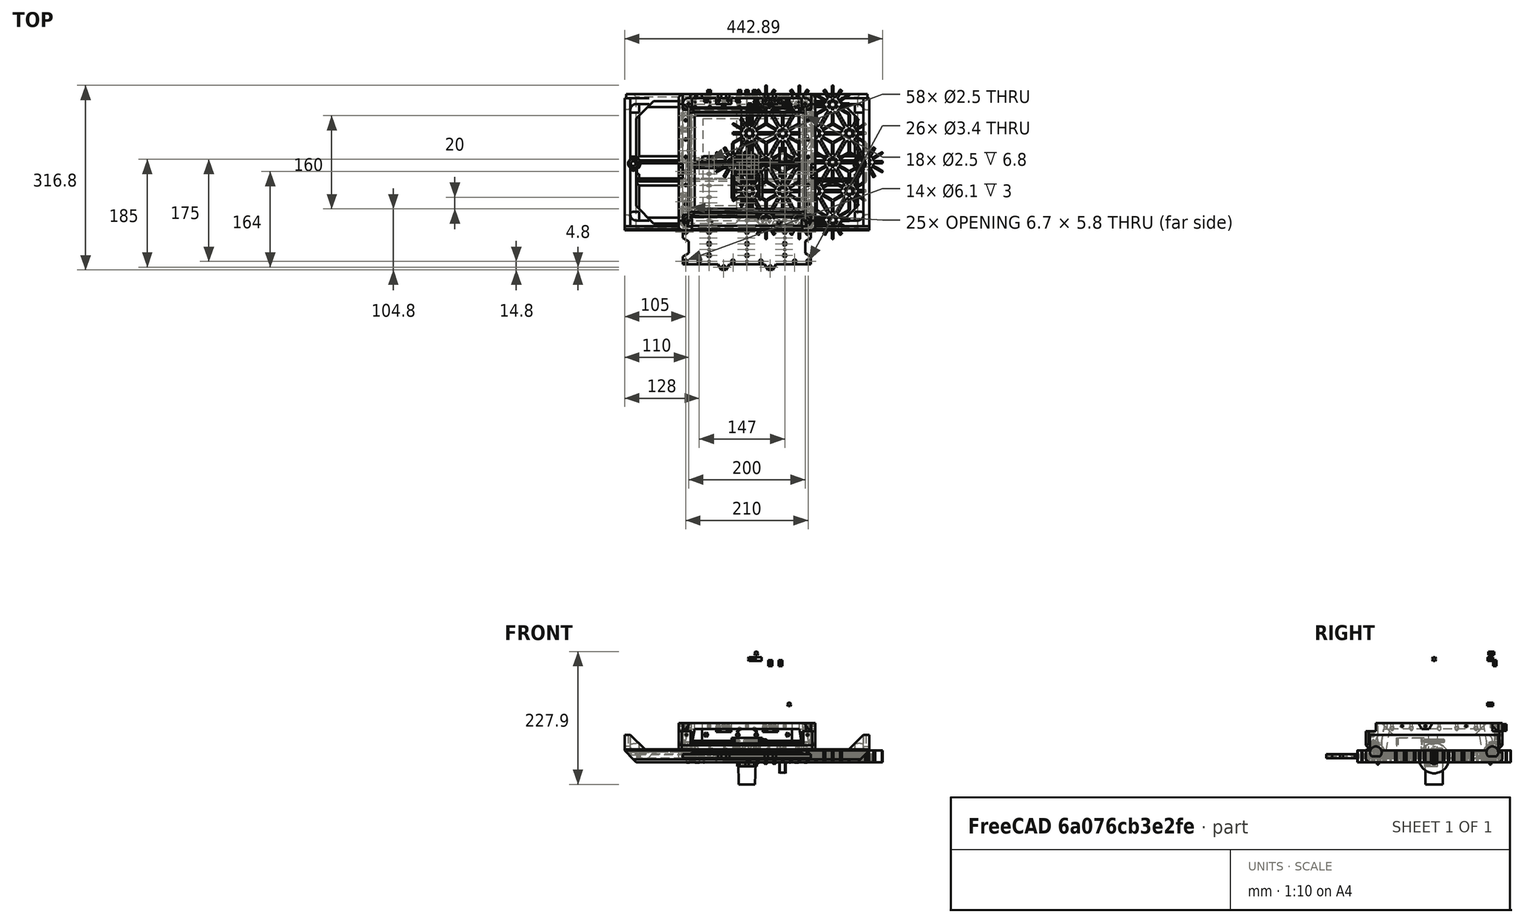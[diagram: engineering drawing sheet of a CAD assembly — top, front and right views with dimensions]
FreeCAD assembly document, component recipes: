
FREECAD ASSEMBLY — COMPONENT RECIPES ("miniXY-Frame")

This assembly document has 23 components, labeled P0..P22 below (a component is one placed body or linked part). 20 of them carry a construction recipe — the FreeCAD feature program that regenerates the part from scratch, quoted from this document or its linked companion documents; the rest are supplied as boundary geometry only. No exploded tour is included for this assembly.
NOTE — document 2 of 3 of this assembly tour. The two overview renders and the header above are repeated from document 1; the component sections below continue where the previous document stopped.
COMPONENT P8 — recipe-attached ("RearPanel", modeled in this document).
Construction recipe (the document's own serialized feature program — sketch geometry with constraints, then the solid features built on it; lengths are millimeters unless a unit is written):

FEATURE [Sketcher::SketchObject] Sketch089
  FullyConstrained = true
  MapMode = 5
  Support = -> [XY_Plane012]
  expr: Constraints[100] = <<Variables>>.FittingGap / 2
  expr: Constraints[101] = <<Variables>>.FittingGap / 2
  expr: Constraints[130] = -<<Variables>>.GantorySpacing / 2
  expr: Constraints[131] = 10 - <<Variables>>.FittingGap
  expr: Constraints[56] = 10 - <<Variables>>.FittingGap
  expr: Constraints[62] = <<Variables>>.FittingGap / 2
  expr: Constraints[63] = <<Variables>>.FittingGap / 2
  expr: Constraints[96] = <<Variables>>.FittingGap / 2
  expr: Constraints[97] = <<Variables>>.FittingGap / 2
  expr: Constraints[98] = <<Variables>>.FittingGap / 2
  expr: Constraints[99] = <<Variables>>.FittingGap / 2
  sketch-geometry (64):
    g0: LineSegment StartX=-109.8 StartY=0 StartZ=0 EndX=-109.8 EndY=-26.242 EndZ=0
    g1: LineSegment StartX=-109.8 StartY=-26.242 StartZ=0 EndX=-100 EndY=-31.9 EndZ=0
    g2: LineSegment StartX=-100 StartY=-52.1 StartZ=0 EndX=-109.8 EndY=-57.758 EndZ=0
    g3: LineSegment StartX=-109.8 StartY=-57.758 StartZ=0 EndX=-109.8 EndY=-78.242 EndZ=0
    g4: LineSegment StartX=-109.8 StartY=-78.242 StartZ=0 EndX=-100 EndY=-83.9 EndZ=0
    g5: LineSegment StartX=-100 StartY=-104.1 StartZ=0 EndX=-109.8 EndY=-109.758 EndZ=0
    g6: LineSegment StartX=-109.8 StartY=-109.758 StartZ=0 EndX=-109.8 EndY=-130.242 EndZ=0
    g7: LineSegment StartX=-109.8 StartY=-130.242 StartZ=0 EndX=-100 EndY=-135.9 EndZ=0
    g8: LineSegment StartX=-100 StartY=-156.1 StartZ=0 EndX=-109.8 EndY=-161.758 EndZ=0
    g9: LineSegment StartX=-109.8 StartY=-161.758 StartZ=0 EndX=-109.8 EndY=-175 EndZ=0
    g10: LineSegment StartX=-49.9 StartY=-175 StartZ=0 EndX=-44.242 EndY=-184.8 EndZ=0
    g11: LineSegment StartX=-44.242 StartY=-184.8 StartZ=0 EndX=-35.758 EndY=-184.8 EndZ=0
    g12: LineSegment StartX=-35.758 StartY=-184.8 StartZ=0 EndX=-30.1 EndY=-175 EndZ=0
    g13: LineSegment StartX=30.1 StartY=-175 StartZ=0 EndX=35.758 EndY=-184.8 EndZ=0
    g14: LineSegment StartX=35.758 StartY=-184.8 StartZ=0 EndX=44.242 EndY=-184.8 EndZ=0
    g15: LineSegment StartX=44.242 StartY=-184.8 StartZ=0 EndX=49.9 EndY=-175 EndZ=0
    g16: LineSegment StartX=49.9 StartY=-175 StartZ=0 EndX=109.8 EndY=-175 EndZ=0
    g17: LineSegment StartX=109.8 StartY=-175 StartZ=0 EndX=109.8 EndY=-161.758 EndZ=0
    g18: LineSegment StartX=109.8 StartY=-161.758 StartZ=0 EndX=100 EndY=-156.1 EndZ=0
    g19: LineSegment StartX=100 StartY=-156.1 StartZ=0 EndX=100 EndY=-135.9 EndZ=0
    g20: LineSegment StartX=100 StartY=-135.9 StartZ=0 EndX=109.8 EndY=-130.242 EndZ=0
    g21: LineSegment StartX=109.8 StartY=-130.242 StartZ=0 EndX=109.8 EndY=-109.758 EndZ=0
    g22: LineSegment StartX=109.8 StartY=-109.758 StartZ=0 EndX=100 EndY=-104.1 EndZ=0
    g23: LineSegment StartX=100 StartY=-104.1 StartZ=0 EndX=100 EndY=-83.9 EndZ=0
    g24: LineSegment StartX=100 StartY=-83.9 StartZ=0 EndX=109.8 EndY=-78.242 EndZ=0
    g25: LineSegment StartX=109.8 StartY=-78.242 StartZ=0 EndX=109.8 EndY=-57.758 EndZ=0
    g26: LineSegment StartX=109.8 StartY=-57.758 StartZ=0 EndX=100 EndY=-52.1 EndZ=0
    g27: LineSegment StartX=100 StartY=-52.1 StartZ=0 EndX=100 EndY=-31.9 EndZ=0
    g28: LineSegment StartX=100 StartY=-31.9 StartZ=0 EndX=109.8 EndY=-26.242 EndZ=0
    g29: LineSegment StartX=109.8 StartY=-26.242 StartZ=0 EndX=109.8 EndY=0 EndZ=0
    g30: LineSegment StartX=109.8 StartY=0 StartZ=0 EndX=-109.8 EndY=0 EndZ=0
    g31: LineSegment StartX=-30.1 StartY=-175 StartZ=0 EndX=30.1 EndY=-175 EndZ=0
    g32: LineSegment StartX=-109.8 StartY=-175 StartZ=0 EndX=-49.9 EndY=-175 EndZ=0
    g33: LineSegment StartX=-100 StartY=-31.9 StartZ=0 EndX=-100 EndY=-52.1 EndZ=0
    g34: LineSegment StartX=-100 StartY=-83.9 StartZ=0 EndX=-100 EndY=-104.1 EndZ=0
    g35: LineSegment StartX=-100 StartY=-135.9 StartZ=0 EndX=-100 EndY=-156.1 EndZ=0
    g36: LineSegment StartX=-100 StartY=0 StartZ=0 EndX=-100 EndY=-235 EndZ=0
    g37: LineSegment StartX=-109.8 StartY=0 StartZ=0 EndX=-109.8 EndY=-235 EndZ=0
    g38: LineSegment StartX=-117.5 StartY=-175 StartZ=0 EndX=117.5 EndY=-175 EndZ=0
    g39: LineSegment StartX=-117.5 StartY=-184.8 StartZ=0 EndX=117.5 EndY=-184.8 EndZ=0
    g40: GeomPoint X=-30 Y=-175 Z=0
    g41: GeomPoint X=-50 Y=-175 Z=0
    g42: GeomPoint X=-100 Y=-32 Z=0
    g43: GeomPoint X=-100 Y=-52 Z=0
    g44: GeomPoint X=-100 Y=-84 Z=0
    g45: GeomPoint X=-100 Y=-104 Z=0
    g46: GeomPoint X=-100 Y=-136 Z=0
    g47: GeomPoint X=-100 Y=-156 Z=0
    g48: Circle CenterX=-40 CenterY=-180 CenterZ=0 NormalX=0 NormalY=0 NormalZ=1 AngleXU=0 Radius=1.5
    g49: Circle CenterX=40 CenterY=-180 CenterZ=0 NormalX=0 NormalY=0 NormalZ=1 AngleXU=0 Radius=1.5
    g50: LineSegment StartX=-117.5 StartY=-170 StartZ=0 EndX=117.5 EndY=-170 EndZ=0
    g51: Circle CenterX=-24 CenterY=-170 CenterZ=0 NormalX=0 NormalY=0 NormalZ=1 AngleXU=0 Radius=1.5
    g52: Circle CenterX=24 CenterY=-170 CenterZ=0 NormalX=0 NormalY=0 NormalZ=1 AngleXU=0 Radius=1.5
    g53: Circle CenterX=-82 CenterY=-170 CenterZ=0 NormalX=0 NormalY=0 NormalZ=1 AngleXU=0 Radius=1.5
    g54: Circle CenterX=82 CenterY=-170 CenterZ=0 NormalX=0 NormalY=0 NormalZ=1 AngleXU=0 Radius=1.5
    g55: LineSegment StartX=-105 StartY=0 StartZ=0 EndX=-105 EndY=-235 EndZ=0
    g56: Circle CenterX=-105 CenterY=-16 CenterZ=0 NormalX=0 NormalY=0 NormalZ=1 AngleXU=0 Radius=1.5
    g57: Circle CenterX=105 CenterY=-16 CenterZ=0 NormalX=0 NormalY=0 NormalZ=1 AngleXU=0 Radius=1.5
    g58: Circle CenterX=-105 CenterY=-68 CenterZ=0 NormalX=0 NormalY=0 NormalZ=1 AngleXU=0 Radius=1.5
    g59: Circle CenterX=105 CenterY=-68 CenterZ=0 NormalX=0 NormalY=0 NormalZ=1 AngleXU=0 Radius=1.5
    g60: Circle CenterX=-105 CenterY=-120 CenterZ=0 NormalX=0 NormalY=0 NormalZ=1 AngleXU=0 Radius=1.5
    g61: Circle CenterX=105 CenterY=-120 CenterZ=0 NormalX=0 NormalY=0 NormalZ=1 AngleXU=0 Radius=1.5
    g62: Circle CenterX=-105 CenterY=-170 CenterZ=0 NormalX=0 NormalY=0 NormalZ=1 AngleXU=0 Radius=1.5
    g63: Circle CenterX=105 CenterY=-170 CenterZ=0 NormalX=0 NormalY=0 NormalZ=1 AngleXU=0 Radius=1.5
  constraints (156):
    c: Coincident(g0,g1)
    c: Coincident(g2,g3)
    c: Coincident(g3,g4)
    c: Coincident(g5,g6)
    c: Coincident(g6,g7)
    c: Coincident(g8,g9)
    c: Coincident(g9,g32)
    c: Coincident(g10,g11)
    c: Coincident(g11,g12)
    c: Coincident(g31,g13)
    c: Coincident(g13,g14)
    c: Coincident(g14,g15)
    c: Coincident(g16,g17)
    c: Coincident(g17,g18)
    c: Coincident(g18,g19)
    c: Coincident(g19,g20)
    c: Coincident(g20,g21)
    c: Coincident(g21,g22)
    c: Coincident(g22,g23)
    c: Coincident(g23,g24)
    c: Coincident(g24,g25)
    c: Coincident(g25,g26)
    c: Coincident(g26,g27)
    c: Coincident(g27,g28)
    c: Coincident(g28,g29)
    c: Coincident(g29,g30)
    c: Coincident(g30,g0)
    c: Parallel(g1,g4)
    c: Parallel(g1,g7)
    c: Parallel(g2,g5)
    c: Parallel(g2,g8)
    c: Symmetric(g0,g29,g-2)
    c: Symmetric(g0,g28,g-2)
    c: Symmetric(g1,g27,g-2)
    c: Symmetric(g2,g26,g-2)
    c: Symmetric(g2,g25,g-2)
    c: Symmetric(g3,g24,g-2)
    c: Symmetric(g4,g23,g-2)
    c: Symmetric(g5,g22,g-2)
    c: Symmetric(g5,g21,g-2)
    c: Symmetric(g6,g20,g-2)
    c: Symmetric(g7,g19,g-2)
    c: Symmetric(g8,g18,g-2)
    c: Symmetric(g8,g17,g-2)
    c: Symmetric(g9,g16,g-2)
    c: Symmetric(g10,g15,g-2)
    c: Symmetric(g10,g14,g-2)
    c: Symmetric(g11,g13,g-2)
    c: Symmetric(g12,g31,g-2)
    c: Angle(g1) = -0.523599
    c: Angle(g2) = -2.61799
    c: Symmetric(g38,g38,g-2)
    c: Symmetric(g39,g39,g-2)
    c: DistanceX(g39,g39) = 235
    c: Equal(g39,g38)
    c: DistanceY(g38) = -175
    c: DistanceY(g39,g38) = 9.8
    c: Coincident(g31,g12)
    c: PointOnObject(g40,g38)
    c: PointOnObject(g41,g38)
    c: DistanceX(g40) = -30
    c: DistanceX(g41,g40) = 20
    c: DistanceX(g41,g10) = 0.1
    c: DistanceX(g12,g40) = 0.1
    c: PointOnObject(g12,g38)
    c: PointOnObject(g11,g39)
    c: PointOnObject(g10,g39)
    c: PointOnObject(g10,g38)
    c: PointOnObject(g9,g38)
    c: PointOnObject(g42,g36)
    c: PointOnObject(g43,g36)
    c: PointOnObject(g44,g36)
    c: PointOnObject(g45,g36)
    c: PointOnObject(g46,g36)
    c: PointOnObject(g47,g36)
    c: Coincident(g1,g33)
    c: Coincident(g33,g2)
    c: Coincident(g4,g34)
    c: Coincident(g5,g34)
    c: Coincident(g7,g35)
    c: Coincident(g8,g35)
    c: PointOnObject(g9,g37)
    c: PointOnObject(g8,g37)
    c: PointOnObject(g6,g37)
    c: PointOnObject(g5,g37)
    c: PointOnObject(g3,g37)
    c: PointOnObject(g2,g37)
    c: PointOnObject(g0,g37)
    c: PointOnObject(g0,g37)
    c: PointOnObject(g0,g-1)
    c: DistanceY(g42) = -32
    c: DistanceY(g43,g42) = 20
    c: DistanceY(g44,g43) = 32
    c: DistanceY(g45,g44) = 20
    c: DistanceY(g46,g45) = 32
    c: DistanceY(g47,g46) = 20
    c: DistanceY(g42,g1) = 0.1
    c: DistanceY(g2,g43) = 0.1
    c: DistanceY(g44,g4) = 0.1
    c: DistanceY(g5,g45) = 0.1
    c: DistanceY(g46,g7) = 0.1
    c: DistanceY(g8,g47) = 0.1
    c: PointOnObject(g1,g36)
    c: PointOnObject(g2,g36)
    c: PointOnObject(g4,g36)
    c: PointOnObject(g5,g36)
    c: PointOnObject(g7,g36)
    c: PointOnObject(g8,g36)
    c: Coincident(g16,g15)
    c: Coincident(g32,g10)
    c: Angle(g12) = 1.0472
    c: Angle(g10) = -1.0472
    c: Symmetric(g48,g49,g-2)
    c: DistanceX(g48) = -40
    c: DistanceY(g48) = -180
    c: Equal(g48,g49)
    c: Diameter(g48) = 3
    c: Symmetric(g50,g50,g-2)
    c: Equal(g39,g50)
    c: DistanceY(g38,g50) = 5
    c: PointOnObject(g51,g50)
    c: PointOnObject(g53,g50)
    c: Symmetric(g51,g52,g-2)
    c: Symmetric(g53,g54,g-2)
    c: DistanceX(g51) = -24
    c: DistanceX(g53) = -82
    c: Equal(g51,g48)
    c: Equal(g52,g48)
    c: Equal(g53,g48)
    c: Equal(g54,g48)
    c: DistanceX(g36) = -100
    c: DistanceX(g37,g36) = 9.8
    c: Vertical(g36)
    c: Vertical(g37)
    c: PointOnObject(g36,g-1)
    c: PointOnObject(g37,g-1)
    c: DistanceY(g37,g37) = 235
    c: Equal(g37,g36)
    c: PointOnObject(g55,g-1)
    c: Vertical(g55)
    c: Equal(g55,g37)
    c: DistanceX(g55,g36) = 5
    c: PointOnObject(g56,g55)
    c: PointOnObject(g58,g55)
    c: PointOnObject(g60,g55)
    c: PointOnObject(g62,g55)
    c: Symmetric(g56,g57,g-2)
    c: Symmetric(g58,g59,g-2)
    c: Symmetric(g60,g61,g-2)
    c: Symmetric(g62,g63,g-2)
    c: DistanceY(g56) = -16
    c: DistanceY(g58,g56) = 52
    c: DistanceY(g60,g58) = 52
    c: PointOnObject(g62,g50)
    c: Equal(g56, g57-g63) x7
    c: Diameter(g56) = 3
FEATURE [PartDesign::Pad] Pad033
  Direction = (0,0,1)
  Length = 7
  Length2 = 10
  Profile = -> Sketch089
  ReferenceAxis = -> Sketch089 [N_Axis]
  Type = 0
  expr: Length = <<Variables>>.WallThickness
FEATURE [PartDesign::SubShapeBinder] Binder009
  BindCopyOnChange = 0
  BindMode = 0
  ClaimChildren = false
  Context = -> Part005 [Body005.Hole034.Binder009.]
  Fuse = false
  MakeFace = true
  OffsetFill = false
  OffsetIntersection = false
  OffsetJoinType = 0
  OffsetOpenResult = false
  PartialLoad = false
  Placement = pos=(0,0,7) rot=(0,0,1;0rad)
  Relative = true
  Support = -> [Pad033[Sketch089.]]
  _Version = 2
  expr: .Placement.Base.z = <<Variables>>.WallThickness
FEATURE [PartDesign::Hole] Hole034
  BaseFeature = -> Pad033
  CustomThreadClearance = 0
  Depth = 25
  DepthType = 0
  Diameter = 3.4
  DrillForDepth = false
  DrillPoint = 1
  DrillPointAngle = 118
  HoleCutCountersinkAngle = 90
  HoleCutCustomValues = false
  HoleCutDepth = 3
  HoleCutDiameter = 6.1
  HoleCutType = 1
  ModelThread = false
  Profile = -> Binder009
  Tapered = false
  TaperedAngle = 90
  ThreadClass = 0
  ThreadDepth = 25
  ThreadDepthType = 0
  ThreadDirection = 0
  ThreadFit = 0
  ThreadSize = 9
  ThreadType = 1
  Threaded = false
  UseCustomThreadClearance = false
FEATURE [Sketcher::SketchObject] Sketch097
  FullyConstrained = true
  MapMode = 5
  Support = -> [XY_Plane012]
  expr: Constraints[153] = <<Variables>>.GantorySpacing - 70
  sketch-geometry (94):
    g0: Circle CenterX=-65 CenterY=-170 CenterZ=0 NormalX=0 NormalY=0 NormalZ=1 AngleXU=0 Radius=1.5
    g1: Circle CenterX=-65 CenterY=-160 CenterZ=0 NormalX=0 NormalY=0 NormalZ=1 AngleXU=0 Radius=1.5
    g2: LineSegment StartX=-65 StartY=-170 StartZ=0 EndX=-65 EndY=-160 EndZ=0
    g3: Circle CenterX=-65 CenterY=-150 CenterZ=0 NormalX=0 NormalY=0 NormalZ=1 AngleXU=0 Radius=1.5
    g4: LineSegment StartX=-65 StartY=-160 StartZ=0 EndX=-65 EndY=-150 EndZ=0
    g5: Circle CenterX=-65 CenterY=-140 CenterZ=0 NormalX=0 NormalY=0 NormalZ=1 AngleXU=0 Radius=1.5
    g6: LineSegment StartX=-65 StartY=-150 StartZ=0 EndX=-65 EndY=-140 EndZ=0
    g7: Circle CenterX=-65 CenterY=-130 CenterZ=0 NormalX=0 NormalY=0 NormalZ=1 AngleXU=0 Radius=1.5
    g8: LineSegment StartX=-65 StartY=-140 StartZ=0 EndX=-65 EndY=-130 EndZ=0
    g9: Circle CenterX=-65 CenterY=-120 CenterZ=0 NormalX=0 NormalY=0 NormalZ=1 AngleXU=0 Radius=1.5
    g10: LineSegment StartX=-65 StartY=-130 StartZ=0 EndX=-65 EndY=-120 EndZ=0
    g11: Circle CenterX=-65 CenterY=-110 CenterZ=0 NormalX=0 NormalY=0 NormalZ=1 AngleXU=0 Radius=1.5
    g12: LineSegment StartX=-65 StartY=-120 StartZ=0 EndX=-65 EndY=-110 EndZ=0
    g13: Circle CenterX=-65 CenterY=-100 CenterZ=0 NormalX=0 NormalY=0 NormalZ=1 AngleXU=0 Radius=1.5
    g14: LineSegment StartX=-65 StartY=-110 StartZ=0 EndX=-65 EndY=-100 EndZ=0
    g15: Circle CenterX=-65 CenterY=-90 CenterZ=0 NormalX=0 NormalY=0 NormalZ=1 AngleXU=0 Radius=1.5
    g16: LineSegment StartX=-65 StartY=-100 StartZ=0 EndX=-65 EndY=-90 EndZ=0
    g17: Circle CenterX=-65 CenterY=-80 CenterZ=0 NormalX=0 NormalY=0 NormalZ=1 AngleXU=0 Radius=1.5
    g18: LineSegment StartX=-65 StartY=-90 StartZ=0 EndX=-65 EndY=-80 EndZ=0
    g19: Circle CenterX=-65 CenterY=-70 CenterZ=0 NormalX=0 NormalY=0 NormalZ=1 AngleXU=0 Radius=1.5
    g20: LineSegment StartX=-65 StartY=-80 StartZ=0 EndX=-65 EndY=-70 EndZ=0
    g21: Circle CenterX=-65 CenterY=-60 CenterZ=0 NormalX=0 NormalY=0 NormalZ=1 AngleXU=0 Radius=1.5
    g22: LineSegment StartX=-65 StartY=-70 StartZ=0 EndX=-65 EndY=-60 EndZ=0
    g23: Circle CenterX=-65 CenterY=-50 CenterZ=0 NormalX=0 NormalY=0 NormalZ=1 AngleXU=0 Radius=1.5
    g24: LineSegment StartX=-65 StartY=-60 StartZ=0 EndX=-65 EndY=-50 EndZ=0
    g25: Circle CenterX=-65 CenterY=-40 CenterZ=0 NormalX=0 NormalY=0 NormalZ=1 AngleXU=0 Radius=1.5
    g26: LineSegment StartX=-65 StartY=-50 StartZ=0 EndX=-65 EndY=-40 EndZ=0
    g27: Circle CenterX=-65 CenterY=-30 CenterZ=0 NormalX=0 NormalY=0 NormalZ=1 AngleXU=0 Radius=1.5
    g28: LineSegment StartX=-65 StartY=-40 StartZ=0 EndX=-65 EndY=-30 EndZ=0
    g29: Circle CenterX=-65 CenterY=-20 CenterZ=0 NormalX=0 NormalY=0 NormalZ=1 AngleXU=0 Radius=1.5
    g30: LineSegment StartX=-65 StartY=-30 StartZ=0 EndX=-65 EndY=-20 EndZ=0
    g31: Circle CenterX=65 CenterY=-170 CenterZ=0 NormalX=0 NormalY=0 NormalZ=1 AngleXU=0 Radius=1.5
    g32: Circle CenterX=65 CenterY=-160 CenterZ=0 NormalX=0 NormalY=0 NormalZ=1 AngleXU=0 Radius=1.5
    g33: LineSegment StartX=65 StartY=-170 StartZ=0 EndX=65 EndY=-160 EndZ=0
    g34: Circle CenterX=65 CenterY=-150 CenterZ=0 NormalX=0 NormalY=0 NormalZ=1 AngleXU=0 Radius=1.5
    g35: LineSegment StartX=65 StartY=-160 StartZ=0 EndX=65 EndY=-150 EndZ=0
    g36: Circle CenterX=65 CenterY=-140 CenterZ=0 NormalX=0 NormalY=0 NormalZ=1 AngleXU=0 Radius=1.5
    g37: LineSegment StartX=65 StartY=-150 StartZ=0 EndX=65 EndY=-140 EndZ=0
    g38: Circle CenterX=65 CenterY=-130 CenterZ=0 NormalX=0 NormalY=0 NormalZ=1 AngleXU=0 Radius=1.5
    g39: LineSegment StartX=65 StartY=-140 StartZ=0 EndX=65 EndY=-130 EndZ=0
    g40: Circle CenterX=65 CenterY=-120 CenterZ=0 NormalX=0 NormalY=0 NormalZ=1 AngleXU=0 Radius=1.5
    g41: LineSegment StartX=65 StartY=-130 StartZ=0 EndX=65 EndY=-120 EndZ=0
    g42: Circle CenterX=65 CenterY=-110 CenterZ=0 NormalX=0 NormalY=0 NormalZ=1 AngleXU=0 Radius=1.5
    g43: LineSegment StartX=65 StartY=-120 StartZ=0 EndX=65 EndY=-110 EndZ=0
    g44: Circle CenterX=65 CenterY=-100 CenterZ=0 NormalX=0 NormalY=0 NormalZ=1 AngleXU=0 Radius=1.5
    g45: LineSegment StartX=65 StartY=-110 StartZ=0 EndX=65 EndY=-100 EndZ=0
    g46: Circle CenterX=65 CenterY=-90 CenterZ=0 NormalX=0 NormalY=0 NormalZ=1 AngleXU=0 Radius=1.5
    g47: LineSegment StartX=65 StartY=-100 StartZ=0 EndX=65 EndY=-90 EndZ=0
    g48: Circle CenterX=65 CenterY=-80 CenterZ=0 NormalX=0 NormalY=0 NormalZ=1 AngleXU=0 Radius=1.5
    g49: LineSegment StartX=65 StartY=-90 StartZ=0 EndX=65 EndY=-80 EndZ=0
    g50: Circle CenterX=65 CenterY=-70 CenterZ=0 NormalX=0 NormalY=0 NormalZ=1 AngleXU=0 Radius=1.5
    g51: LineSegment StartX=65 StartY=-80 StartZ=0 EndX=65 EndY=-70 EndZ=0
    g52: Circle CenterX=65 CenterY=-60 CenterZ=0 NormalX=0 NormalY=0 NormalZ=1 AngleXU=0 Radius=1.5
    g53: LineSegment StartX=65 StartY=-70 StartZ=0 EndX=65 EndY=-60 EndZ=0
    g54: Circle CenterX=65 CenterY=-50 CenterZ=0 NormalX=0 NormalY=0 NormalZ=1 AngleXU=0 Radius=1.5
    g55: LineSegment StartX=65 StartY=-60 StartZ=0 EndX=65 EndY=-50 EndZ=0
    g56: Circle CenterX=65 CenterY=-40 CenterZ=0 NormalX=0 NormalY=0 NormalZ=1 AngleXU=0 Radius=1.5
    g57: LineSegment StartX=65 StartY=-50 StartZ=0 EndX=65 EndY=-40 EndZ=0
    g58: Circle CenterX=65 CenterY=-30 CenterZ=0 NormalX=0 NormalY=0 NormalZ=1 AngleXU=0 Radius=1.5
    g59: LineSegment StartX=65 StartY=-40 StartZ=0 EndX=65 EndY=-30 EndZ=0
    g60: Circle CenterX=65 CenterY=-20 CenterZ=0 NormalX=0 NormalY=0 NormalZ=1 AngleXU=0 Radius=1.5
    g61: LineSegment StartX=65 StartY=-30 StartZ=0 EndX=65 EndY=-20 EndZ=0
    g62: Circle CenterX=0 CenterY=-170 CenterZ=0 NormalX=0 NormalY=0 NormalZ=1 AngleXU=0 Radius=1.5
    g63: Circle CenterX=6e-16 CenterY=-160 CenterZ=0 NormalX=0 NormalY=0 NormalZ=1 AngleXU=0 Radius=1.5
    g64: LineSegment StartX=0 StartY=-170 StartZ=0 EndX=6e-16 EndY=-160 EndZ=0
    g65: Circle CenterX=1.2e-15 CenterY=-150 CenterZ=0 NormalX=0 NormalY=0 NormalZ=1 AngleXU=0 Radius=1.5
    g66: LineSegment StartX=6e-16 StartY=-160 StartZ=0 EndX=1.2e-15 EndY=-150 EndZ=0
    g67: Circle CenterX=1.8e-15 CenterY=-140 CenterZ=0 NormalX=0 NormalY=0 NormalZ=1 AngleXU=0 Radius=1.5
    g68: LineSegment StartX=1.2e-15 StartY=-150 StartZ=0 EndX=1.8e-15 EndY=-140 EndZ=0
    g69: Circle CenterX=2.4e-15 CenterY=-130 CenterZ=0 NormalX=0 NormalY=0 NormalZ=1 AngleXU=0 Radius=1.5
    g70: LineSegment StartX=1.8e-15 StartY=-140 StartZ=0 EndX=2.4e-15 EndY=-130 EndZ=0
    g71: Circle CenterX=3.1e-15 CenterY=-120 CenterZ=0 NormalX=0 NormalY=0 NormalZ=1 AngleXU=0 Radius=1.5
    g72: LineSegment StartX=2.4e-15 StartY=-130 StartZ=0 EndX=3.1e-15 EndY=-120 EndZ=0
    g73: Circle CenterX=3.7e-15 CenterY=-110 CenterZ=0 NormalX=0 NormalY=0 NormalZ=1 AngleXU=0 Radius=1.5
    g74: LineSegment StartX=3.1e-15 StartY=-120 StartZ=0 EndX=3.7e-15 EndY=-110 EndZ=0
    g75: Circle CenterX=4.3e-15 CenterY=-100 CenterZ=0 NormalX=0 NormalY=0 NormalZ=1 AngleXU=0 Radius=1.5
    g76: LineSegment StartX=3.7e-15 StartY=-110 StartZ=0 EndX=4.3e-15 EndY=-100 EndZ=0
    g77: Circle CenterX=4.9e-15 CenterY=-90 CenterZ=0 NormalX=0 NormalY=0 NormalZ=1 AngleXU=0 Radius=1.5
    g78: LineSegment StartX=4.3e-15 StartY=-100 StartZ=0 EndX=4.9e-15 EndY=-90 EndZ=0
    g79: Circle CenterX=5.5e-15 CenterY=-80 CenterZ=0 NormalX=0 NormalY=0 NormalZ=1 AngleXU=0 Radius=1.5
    g80: LineSegment StartX=4.9e-15 StartY=-90 StartZ=0 EndX=5.5e-15 EndY=-80 EndZ=0
    g81: Circle CenterX=6.1e-15 CenterY=-70 CenterZ=0 NormalX=0 NormalY=0 NormalZ=1 AngleXU=0 Radius=1.5
    g82: LineSegment StartX=5.5e-15 StartY=-80 StartZ=0 EndX=6.1e-15 EndY=-70 EndZ=0
    g83: Circle CenterX=6.7e-15 CenterY=-60 CenterZ=0 NormalX=0 NormalY=0 NormalZ=1 AngleXU=0 Radius=1.5
    g84: LineSegment StartX=6.1e-15 StartY=-70 StartZ=0 EndX=6.7e-15 EndY=-60 EndZ=0
    g85: Circle CenterX=7.3e-15 CenterY=-50 CenterZ=0 NormalX=0 NormalY=0 NormalZ=1 AngleXU=0 Radius=1.5
    g86: LineSegment StartX=6.7e-15 StartY=-60 StartZ=0 EndX=7.3e-15 EndY=-50 EndZ=0
    g87: Circle CenterX=8e-15 CenterY=-40 CenterZ=0 NormalX=0 NormalY=0 NormalZ=1 AngleXU=0 Radius=1.5
    g88: LineSegment StartX=7.3e-15 StartY=-50 StartZ=0 EndX=8e-15 EndY=-40 EndZ=0
    g89: Circle CenterX=8.6e-15 CenterY=-30 CenterZ=0 NormalX=0 NormalY=0 NormalZ=1 AngleXU=0 Radius=1.5
    g90: LineSegment StartX=8e-15 StartY=-40 StartZ=0 EndX=8.6e-15 EndY=-30 EndZ=0
    g91: Circle CenterX=9.2e-15 CenterY=-20 CenterZ=0 NormalX=0 NormalY=0 NormalZ=1 AngleXU=0 Radius=1.5
    g92: LineSegment StartX=8.6e-15 StartY=-30 StartZ=0 EndX=9.2e-15 EndY=-20 EndZ=0
    g93: LineSegment StartX=-117.5 StartY=-170 StartZ=0 EndX=117.5 EndY=-170 EndZ=0
  constraints (236):
    c: Diameter(g0) = 3
    c: Diameter(g1) = 3
    c: Coincident(g0,g2)
    c: Coincident(g1,g2)
    c: Distance(g2) = 10
    c: Angle(g2) = 1.5708
    c: Diameter(g3) = 3
    c: Coincident(g1,g4)
    c: Coincident(g3,g4)
    c: Equal(g2,g4)
    c: Parallel(g4,g2)
    c: Diameter(g5) = 3
    c: Coincident(g3,g6)
    c: Coincident(g5,g6)
    c: Equal(g2,g6)
    c: Parallel(g6,g2)
    c: Diameter(g7) = 3
    c: Coincident(g5,g8)
    c: Coincident(g7,g8)
    c: Equal(g2,g8)
    c: Parallel(g8,g2)
    c: Diameter(g9) = 3
    c: Coincident(g7,g10)
    c: Coincident(g9,g10)
    c: Equal(g2,g10)
    c: Parallel(g10,g2)
    c: Diameter(g11) = 3
    c: Coincident(g9,g12)
    c: Coincident(g11,g12)
    c: Equal(g2,g12)
    c: Parallel(g12,g2)
    c: Diameter(g13) = 3
    c: Coincident(g11,g14)
    c: Coincident(g13,g14)
    c: Equal(g2,g14)
    c: Parallel(g14,g2)
    c: Diameter(g15) = 3
    c: Coincident(g13,g16)
    c: Coincident(g15,g16)
    c: Equal(g2,g16)
    c: Parallel(g16,g2)
    c: Diameter(g17) = 3
    c: Coincident(g15,g18)
    c: Coincident(g17,g18)
    c: Equal(g2,g18)
    c: Parallel(g18,g2)
    c: Diameter(g19) = 3
    c: Coincident(g17,g20)
    c: Coincident(g19,g20)
    c: Equal(g2,g20)
    c: Parallel(g20,g2)
    c: Diameter(g21) = 3
    c: Coincident(g19,g22)
    c: Coincident(g21,g22)
    c: Equal(g2,g22)
    c: Parallel(g22,g2)
    c: Diameter(g23) = 3
    c: Coincident(g21,g24)
    c: Coincident(g23,g24)
    c: Equal(g2,g24)
    c: Parallel(g24,g2)
    c: Diameter(g25) = 3
    c: Coincident(g23,g26)
    c: Coincident(g25,g26)
    c: Equal(g2,g26)
    c: Parallel(g26,g2)
    c: Diameter(g27) = 3
    c: Coincident(g25,g28)
    c: Coincident(g27,g28)
    c: Equal(g2,g28)
    c: Parallel(g28,g2)
    c: Diameter(g29) = 3
    c: Coincident(g27,g30)
    c: Coincident(g29,g30)
    c: Equal(g2,g30)
    c: Parallel(g30,g2)
    c: Diameter(g31) = 3
    c: Diameter(g32) = 3
    c: Coincident(g31,g33)
    c: Coincident(g32,g33)
    c: Distance(g33) = 10
    c: Angle(g33) = 1.5708
    c: Diameter(g34) = 3
    c: Coincident(g32,g35)
    c: Coincident(g34,g35)
    c: Equal(g33,g35)
    c: Parallel(g35,g33)
    c: Diameter(g36) = 3
    c: Coincident(g34,g37)
    c: Coincident(g36,g37)
    c: Equal(g33,g37)
    c: Parallel(g37,g33)
    c: Diameter(g38) = 3
    c: Coincident(g36,g39)
    c: Coincident(g38,g39)
    c: Equal(g33,g39)
    c: Parallel(g39,g33)
    c: Diameter(g40) = 3
    c: Coincident(g38,g41)
    c: Coincident(g40,g41)
    c: Equal(g33,g41)
    c: Parallel(g41,g33)
    c: Diameter(g42) = 3
    c: Coincident(g40,g43)
    c: Coincident(g42,g43)
    c: Equal(g33,g43)
    c: Parallel(g43,g33)
    c: Diameter(g44) = 3
    c: Coincident(g42,g45)
    c: Coincident(g44,g45)
    c: Equal(g33,g45)
    c: Parallel(g45,g33)
    c: Diameter(g46) = 3
    c: Coincident(g44,g47)
    c: Coincident(g46,g47)
    c: Equal(g33,g47)
    c: Parallel(g47,g33)
    c: Diameter(g48) = 3
    c: Coincident(g46,g49)
    c: Coincident(g48,g49)
    c: Equal(g33,g49)
    c: Parallel(g49,g33)
    c: Diameter(g50) = 3
    c: Coincident(g48,g51)
    c: Coincident(g50,g51)
    c: Equal(g33,g51)
    c: Parallel(g51,g33)
    c: Diameter(g52) = 3
    c: Coincident(g50,g53)
    c: Coincident(g52,g53)
    c: Equal(g33,g53)
    c: Parallel(g53,g33)
    c: Diameter(g54) = 3
    c: Coincident(g52,g55)
    c: Coincident(g54,g55)
    c: Equal(g33,g55)
    c: Parallel(g55,g33)
    c: Diameter(g56) = 3
    c: Coincident(g54,g57)
    c: Coincident(g56,g57)
    c: Equal(g33,g57)
    c: Parallel(g57,g33)
    c: Diameter(g58) = 3
    c: Coincident(g56,g59)
    c: Coincident(g58,g59)
    c: Equal(g33,g59)
    c: Parallel(g59,g33)
    c: Diameter(g60) = 3
    c: Coincident(g58,g61)
    c: Coincident(g60,g61)
    c: Equal(g33,g61)
    c: Parallel(g61,g33)
    c: Symmetric(g0,g31,g-2)
    c: DistanceX(g0,g31) = 130
    c: Diameter(g62) = 3
    c: Diameter(g63) = 3
    c: Coincident(g62,g64)
    c: Coincident(g63,g64)
    c: Distance(g64) = 10
    c: Angle(g64) = 1.5708
    c: Diameter(g65) = 3
    c: Coincident(g63,g66)
    c: Coincident(g65,g66)
    c: Equal(g64,g66)
    c: Parallel(g66,g64)
    c: Diameter(g67) = 3
    c: Coincident(g65,g68)
    c: Coincident(g67,g68)
    c: Equal(g64,g68)
    c: Parallel(g68,g64)
    c: Diameter(g69) = 3
    c: Coincident(g67,g70)
    c: Coincident(g69,g70)
    c: Equal(g64,g70)
    c: Parallel(g70,g64)
    c: Diameter(g71) = 3
    c: Coincident(g69,g72)
    c: Coincident(g71,g72)
    c: Equal(g64,g72)
    c: Parallel(g72,g64)
    c: Diameter(g73) = 3
    c: Coincident(g71,g74)
    c: Coincident(g73,g74)
    c: Equal(g64,g74)
    c: Parallel(g74,g64)
    c: Diameter(g75) = 3
    c: Coincident(g73,g76)
    c: Coincident(g75,g76)
    c: Equal(g64,g76)
    c: Parallel(g76,g64)
    c: Diameter(g77) = 3
    c: Coincident(g75,g78)
    c: Coincident(g77,g78)
    c: Equal(g64,g78)
    c: Parallel(g78,g64)
    c: Diameter(g79) = 3
    c: Coincident(g77,g80)
    c: Coincident(g79,g80)
    c: Equal(g64,g80)
    c: Parallel(g80,g64)
    c: Diameter(g81) = 3
    c: Coincident(g79,g82)
    c: Coincident(g81,g82)
    c: Equal(g64,g82)
    c: Parallel(g82,g64)
    c: Diameter(g83) = 3
    c: Coincident(g81,g84)
    c: Coincident(g83,g84)
    c: Equal(g64,g84)
    c: Parallel(g84,g64)
    c: Diameter(g85) = 3
    c: Coincident(g83,g86)
    c: Coincident(g85,g86)
    c: Equal(g64,g86)
    c: Parallel(g86,g64)
    c: Diameter(g87) = 3
    c: Coincident(g85,g88)
    c: Coincident(g87,g88)
    c: Equal(g64,g88)
    c: Parallel(g88,g64)
    c: Diameter(g89) = 3
    c: Coincident(g87,g90)
    c: Coincident(g89,g90)
    c: Equal(g64,g90)
    c: Parallel(g90,g64)
    c: Diameter(g91) = 3
    c: Coincident(g89,g92)
    c: Coincident(g91,g92)
    c: Equal(g64,g92)
    c: Parallel(g92,g64)
    c: PointOnObject(g62,g-2)
    c: Symmetric(g93,g93,g-2)
    c: DistanceX(g93,g93) = 235
    c: DistanceY(g93) = -170
    c: PointOnObject(g0,g93)
    c: PointOnObject(g62,g93)
FEATURE [PartDesign::Hole] Hole035
  BaseFeature = -> Hole034
  CustomThreadClearance = 0
  Depth = 25
  DepthType = 0
  Diameter = 2.5
  DrillForDepth = false
  DrillPoint = 1
  DrillPointAngle = 118
  HoleCutCountersinkAngle = 90
  HoleCutCustomValues = false
  HoleCutDepth = 0
  HoleCutDiameter = 6.1
  HoleCutType = 0
  ModelThread = false
  Profile = -> Sketch097
  Reversed = true
  Tapered = false
  TaperedAngle = 90
  ThreadClass = 0
  ThreadDepth = 25
  ThreadDepthType = 0
  ThreadDirection = 0
  ThreadFit = 0
  ThreadSize = 9
  ThreadType = 1
  Threaded = true
  UseCustomThreadClearance = false
FEATURE [Sketcher::SketchObject] Sketch099
  AttachmentOffset = pos=(0,0,4) rot=(0,0,1;0rad)
  FullyConstrained = true
  MapMode = 5
  Placement = pos=(0,0,4) rot=(0,0,1;0rad)
  Support = -> [XY_Plane012]
  expr: .AttachmentOffset.Base.z = <<Variables>>.WallThickness - 3
  sketch-geometry (185):
    g0: LineSegment StartX=-150 StartY=-160 StartZ=0 EndX=150 EndY=-160 EndZ=0
    g1: LineSegment StartX=-65 StartY=0 StartZ=0 EndX=-65 EndY=-160 EndZ=0
    g2: LineSegment StartX=65 StartY=0 StartZ=0 EndX=65 EndY=-160 EndZ=0
    g3: LineSegment StartX=-150 StartY=-140 StartZ=0 EndX=150 EndY=-140 EndZ=0
    g4: LineSegment StartX=-150 StartY=-160 StartZ=0 EndX=-150 EndY=-140 EndZ=0
    g5: LineSegment StartX=-150 StartY=-120 StartZ=0 EndX=150 EndY=-120 EndZ=0
    g6: LineSegment StartX=-150 StartY=-140 StartZ=0 EndX=-150 EndY=-120 EndZ=0
    g7: LineSegment StartX=-150 StartY=-100 StartZ=0 EndX=150 EndY=-100 EndZ=0
    g8: LineSegment StartX=-150 StartY=-120 StartZ=0 EndX=-150 EndY=-100 EndZ=0
    g9: LineSegment StartX=-150 StartY=-80 StartZ=0 EndX=150 EndY=-80 EndZ=0
    g10: LineSegment StartX=-150 StartY=-100 StartZ=0 EndX=-150 EndY=-80 EndZ=0
    g11: LineSegment StartX=-150 StartY=-60 StartZ=0 EndX=150 EndY=-60 EndZ=0
    g12: LineSegment StartX=-150 StartY=-80 StartZ=0 EndX=-150 EndY=-60 EndZ=0
    g13: LineSegment StartX=-150 StartY=-40 StartZ=0 EndX=150 EndY=-40 EndZ=0
    g14: LineSegment StartX=-150 StartY=-60 StartZ=0 EndX=-150 EndY=-40 EndZ=0
    g15: LineSegment StartX=-150 StartY=-20 StartZ=0 EndX=150 EndY=-20 EndZ=0
    g16: LineSegment StartX=-150 StartY=-40 StartZ=0 EndX=-150 EndY=-20 EndZ=0
    g17: LineSegment StartX=-65 StartY=-156.65 StartZ=0 EndX=-67.9012 EndY=-158.325 EndZ=0
    g18: LineSegment StartX=-67.9012 StartY=-158.325 StartZ=0 EndX=-67.9012 EndY=-161.675 EndZ=0
    g19: LineSegment StartX=-67.9012 StartY=-161.675 StartZ=0 EndX=-65 EndY=-163.35 EndZ=0
    g20: LineSegment StartX=-65 StartY=-163.35 StartZ=0 EndX=-62.0988 EndY=-161.675 EndZ=0
    g21: LineSegment StartX=-62.0988 StartY=-161.675 StartZ=0 EndX=-62.0988 EndY=-158.325 EndZ=0
    g22: LineSegment StartX=-62.0988 StartY=-158.325 StartZ=0 EndX=-65 EndY=-156.65 EndZ=0
    g23: Circle CenterX=-65 CenterY=-160 CenterZ=0 NormalX=0 NormalY=0 NormalZ=1 AngleXU=0 Radius=3.35
    g24: LineSegment StartX=-65 StartY=-136.65 StartZ=0 EndX=-67.9012 EndY=-138.325 EndZ=0
    g25: LineSegment StartX=-67.9012 StartY=-138.325 StartZ=0 EndX=-67.9012 EndY=-141.675 EndZ=0
    g26: LineSegment StartX=-67.9012 StartY=-141.675 StartZ=0 EndX=-65 EndY=-143.35 EndZ=0
    g27: LineSegment StartX=-65 StartY=-143.35 StartZ=0 EndX=-62.0988 EndY=-141.675 EndZ=0
    g28: LineSegment StartX=-62.0988 StartY=-141.675 StartZ=0 EndX=-62.0988 EndY=-138.325 EndZ=0
    g29: LineSegment StartX=-62.0988 StartY=-138.325 StartZ=0 EndX=-65 EndY=-136.65 EndZ=0
    g30: Circle CenterX=-65 CenterY=-140 CenterZ=0 NormalX=0 NormalY=0 NormalZ=1 AngleXU=0 Radius=3.35
    g31: LineSegment StartX=-65 StartY=-116.65 StartZ=0 EndX=-67.9012 EndY=-118.325 EndZ=0
    g32: LineSegment StartX=-67.9012 StartY=-118.325 StartZ=0 EndX=-67.9012 EndY=-121.675 EndZ=0
    g33: LineSegment StartX=-67.9012 StartY=-121.675 StartZ=0 EndX=-65 EndY=-123.35 EndZ=0
    g34: LineSegment StartX=-65 StartY=-123.35 StartZ=0 EndX=-62.0988 EndY=-121.675 EndZ=0
    g35: LineSegment StartX=-62.0988 StartY=-121.675 StartZ=0 EndX=-62.0988 EndY=-118.325 EndZ=0
    g36: LineSegment StartX=-62.0988 StartY=-118.325 StartZ=0 EndX=-65 EndY=-116.65 EndZ=0
    g37: Circle CenterX=-65 CenterY=-120 CenterZ=0 NormalX=0 NormalY=0 NormalZ=1 AngleXU=0 Radius=3.35
    g38: LineSegment StartX=-65 StartY=-96.65 StartZ=0 EndX=-67.9012 EndY=-98.325 EndZ=0
    g39: LineSegment StartX=-67.9012 StartY=-98.325 StartZ=0 EndX=-67.9012 EndY=-101.675 EndZ=0
    g40: LineSegment StartX=-67.9012 StartY=-101.675 StartZ=0 EndX=-65 EndY=-103.35 EndZ=0
    g41: LineSegment StartX=-65 StartY=-103.35 StartZ=0 EndX=-62.0988 EndY=-101.675 EndZ=0
    g42: LineSegment StartX=-62.0988 StartY=-101.675 StartZ=0 EndX=-62.0988 EndY=-98.325 EndZ=0
    g43: LineSegment StartX=-62.0988 StartY=-98.325 StartZ=0 EndX=-65 EndY=-96.65 EndZ=0
    g44: Circle CenterX=-65 CenterY=-100 CenterZ=0 NormalX=0 NormalY=0 NormalZ=1 AngleXU=0 Radius=3.35
    g45: LineSegment StartX=-65 StartY=-76.65 StartZ=0 EndX=-67.9012 EndY=-78.325 EndZ=0
    g46: LineSegment StartX=-67.9012 StartY=-78.325 StartZ=0 EndX=-67.9012 EndY=-81.675 EndZ=0
    g47: LineSegment StartX=-67.9012 StartY=-81.675 StartZ=0 EndX=-65 EndY=-83.35 EndZ=0
    g48: LineSegment StartX=-65 StartY=-83.35 StartZ=0 EndX=-62.0988 EndY=-81.675 EndZ=0
    g49: LineSegment StartX=-62.0988 StartY=-81.675 StartZ=0 EndX=-62.0988 EndY=-78.325 EndZ=0
    g50: LineSegment StartX=-62.0988 StartY=-78.325 StartZ=0 EndX=-65 EndY=-76.65 EndZ=0
    g51: Circle CenterX=-65 CenterY=-80 CenterZ=0 NormalX=0 NormalY=0 NormalZ=1 AngleXU=0 Radius=3.35
    g52: LineSegment StartX=-65 StartY=-56.65 StartZ=0 EndX=-67.9012 EndY=-58.325 EndZ=0
    g53: LineSegment StartX=-67.9012 StartY=-58.325 StartZ=0 EndX=-67.9012 EndY=-61.675 EndZ=0
    g54: LineSegment StartX=-67.9012 StartY=-61.675 StartZ=0 EndX=-65 EndY=-63.35 EndZ=0
    g55: LineSegment StartX=-65 StartY=-63.35 StartZ=0 EndX=-62.0988 EndY=-61.675 EndZ=0
    g56: LineSegment StartX=-62.0988 StartY=-61.675 StartZ=0 EndX=-62.0988 EndY=-58.325 EndZ=0
    g57: LineSegment StartX=-62.0988 StartY=-58.325 StartZ=0 EndX=-65 EndY=-56.65 EndZ=0
    g58: Circle CenterX=-65 CenterY=-60 CenterZ=0 NormalX=0 NormalY=0 NormalZ=1 AngleXU=0 Radius=3.35
    g59: LineSegment StartX=-65 StartY=-36.65 StartZ=0 EndX=-67.9012 EndY=-38.325 EndZ=0
    g60: LineSegment StartX=-67.9012 StartY=-38.325 StartZ=0 EndX=-67.9012 EndY=-41.675 EndZ=0
    g61: LineSegment StartX=-67.9012 StartY=-41.675 StartZ=0 EndX=-65 EndY=-43.35 EndZ=0
    g62: LineSegment StartX=-65 StartY=-43.35 StartZ=0 EndX=-62.0988 EndY=-41.675 EndZ=0
    g63: LineSegment StartX=-62.0988 StartY=-41.675 StartZ=0 EndX=-62.0988 EndY=-38.325 EndZ=0
    g64: LineSegment StartX=-62.0988 StartY=-38.325 StartZ=0 EndX=-65 EndY=-36.65 EndZ=0
    g65: Circle CenterX=-65 CenterY=-40 CenterZ=0 NormalX=0 NormalY=0 NormalZ=1 AngleXU=0 Radius=3.35
    g66: LineSegment StartX=-65 StartY=-16.65 StartZ=0 EndX=-67.9012 EndY=-18.325 EndZ=0
    g67: LineSegment StartX=-67.9012 StartY=-18.325 StartZ=0 EndX=-67.9012 EndY=-21.675 EndZ=0
    g68: LineSegment StartX=-67.9012 StartY=-21.675 StartZ=0 EndX=-65 EndY=-23.35 EndZ=0
    g69: LineSegment StartX=-65 StartY=-23.35 StartZ=0 EndX=-62.0988 EndY=-21.675 EndZ=0
    g70: LineSegment StartX=-62.0988 StartY=-21.675 StartZ=0 EndX=-62.0988 EndY=-18.325 EndZ=0
    g71: LineSegment StartX=-62.0988 StartY=-18.325 StartZ=0 EndX=-65 EndY=-16.65 EndZ=0
    g72: Circle CenterX=-65 CenterY=-20 CenterZ=0 NormalX=0 NormalY=0 NormalZ=1 AngleXU=0 Radius=3.35
    g73: LineSegment StartX=0 StartY=-156.65 StartZ=0 EndX=-2.90119 EndY=-158.325 EndZ=0
    g74: LineSegment StartX=-2.90119 StartY=-158.325 StartZ=0 EndX=-2.90119 EndY=-161.675 EndZ=0
    g75: LineSegment StartX=-2.90119 StartY=-161.675 StartZ=0 EndX=0 EndY=-163.35 EndZ=0
    g76: LineSegment StartX=0 StartY=-163.35 StartZ=0 EndX=2.90119 EndY=-161.675 EndZ=0
    g77: LineSegment StartX=2.90119 StartY=-161.675 StartZ=0 EndX=2.90119 EndY=-158.325 EndZ=0
    g78: LineSegment StartX=2.90119 StartY=-158.325 StartZ=0 EndX=0 EndY=-156.65 EndZ=0
    g79: Circle CenterX=0 CenterY=-160 CenterZ=0 NormalX=0 NormalY=0 NormalZ=1 AngleXU=0 Radius=3.35
    g80: LineSegment StartX=0 StartY=-136.65 StartZ=0 EndX=-2.90119 EndY=-138.325 EndZ=0
    g81: LineSegment StartX=-2.90119 StartY=-138.325 StartZ=0 EndX=-2.90119 EndY=-141.675 EndZ=0
    g82: LineSegment StartX=-2.90119 StartY=-141.675 StartZ=0 EndX=0 EndY=-143.35 EndZ=0
    g83: LineSegment StartX=0 StartY=-143.35 StartZ=0 EndX=2.90119 EndY=-141.675 EndZ=0
    g84: LineSegment StartX=2.90119 StartY=-141.675 StartZ=0 EndX=2.90119 EndY=-138.325 EndZ=0
    g85: LineSegment StartX=2.90119 StartY=-138.325 StartZ=0 EndX=0 EndY=-136.65 EndZ=0
    g86: Circle CenterX=0 CenterY=-140 CenterZ=0 NormalX=0 NormalY=0 NormalZ=1 AngleXU=0 Radius=3.35
    g87: LineSegment StartX=0 StartY=-116.65 StartZ=0 EndX=-2.90119 EndY=-118.325 EndZ=0
    g88: LineSegment StartX=-2.90119 StartY=-118.325 StartZ=0 EndX=-2.90119 EndY=-121.675 EndZ=0
    g89: LineSegment StartX=-2.90119 StartY=-121.675 StartZ=0 EndX=0 EndY=-123.35 EndZ=0
    g90: LineSegment StartX=0 StartY=-123.35 StartZ=0 EndX=2.90119 EndY=-121.675 EndZ=0
    g91: LineSegment StartX=2.90119 StartY=-121.675 StartZ=0 EndX=2.90119 EndY=-118.325 EndZ=0
    g92: LineSegment StartX=2.90119 StartY=-118.325 StartZ=0 EndX=0 EndY=-116.65 EndZ=0
    g93: Circle CenterX=0 CenterY=-120 CenterZ=0 NormalX=0 NormalY=0 NormalZ=1 AngleXU=0 Radius=3.35
    g94: LineSegment StartX=0 StartY=-96.65 StartZ=0 EndX=-2.90119 EndY=-98.325 EndZ=0
    g95: LineSegment StartX=-2.90119 StartY=-98.325 StartZ=0 EndX=-2.90119 EndY=-101.675 EndZ=0
    g96: LineSegment StartX=-2.90119 StartY=-101.675 StartZ=0 EndX=4e-16 EndY=-103.35 EndZ=0
    g97: LineSegment StartX=4e-16 StartY=-103.35 StartZ=0 EndX=2.90119 EndY=-101.675 EndZ=0
    g98: LineSegment StartX=2.90119 StartY=-101.675 StartZ=0 EndX=2.90119 EndY=-98.325 EndZ=0
    g99: LineSegment StartX=2.90119 StartY=-98.325 StartZ=0 EndX=0 EndY=-96.65 EndZ=0
    g100: Circle CenterX=0 CenterY=-100 CenterZ=0 NormalX=0 NormalY=0 NormalZ=1 AngleXU=0 Radius=3.35
    g101: LineSegment StartX=0 StartY=-76.65 StartZ=0 EndX=-2.90119 EndY=-78.325 EndZ=0
    g102: LineSegment StartX=-2.90119 StartY=-78.325 StartZ=0 EndX=-2.90119 EndY=-81.675 EndZ=0
    g103: LineSegment StartX=-2.90119 StartY=-81.675 StartZ=0 EndX=0 EndY=-83.35 EndZ=0
    g104: LineSegment StartX=0 StartY=-83.35 StartZ=0 EndX=2.90119 EndY=-81.675 EndZ=0
    g105: LineSegment StartX=2.90119 StartY=-81.675 StartZ=0 EndX=2.90119 EndY=-78.325 EndZ=0
    g106: LineSegment StartX=2.90119 StartY=-78.325 StartZ=0 EndX=0 EndY=-76.65 EndZ=0
    g107: Circle CenterX=0 CenterY=-80 CenterZ=0 NormalX=0 NormalY=0 NormalZ=1 AngleXU=0 Radius=3.35
    g108: LineSegment StartX=0 StartY=-56.65 StartZ=0 EndX=-2.90119 EndY=-58.325 EndZ=0
    g109: LineSegment StartX=-2.90119 StartY=-58.325 StartZ=0 EndX=-2.90119 EndY=-61.675 EndZ=0
    g110: LineSegment StartX=-2.90119 StartY=-61.675 StartZ=0 EndX=4e-16 EndY=-63.35 EndZ=0
    g111: LineSegment StartX=4e-16 StartY=-63.35 StartZ=0 EndX=2.90119 EndY=-61.675 EndZ=0
    g112: LineSegment StartX=2.90119 StartY=-61.675 StartZ=0 EndX=2.90119 EndY=-58.325 EndZ=0
    g113: LineSegment StartX=2.90119 StartY=-58.325 StartZ=0 EndX=0 EndY=-56.65 EndZ=0
    g114: Circle CenterX=0 CenterY=-60 CenterZ=0 NormalX=0 NormalY=0 NormalZ=1 AngleXU=0 Radius=3.35
    g115: LineSegment StartX=0 StartY=-36.65 StartZ=0 EndX=-2.90119 EndY=-38.325 EndZ=0
    g116: LineSegment StartX=-2.90119 StartY=-38.325 StartZ=0 EndX=-2.90119 EndY=-41.675 EndZ=0
    g117: LineSegment StartX=-2.90119 StartY=-41.675 StartZ=0 EndX=4e-16 EndY=-43.35 EndZ=0
    g118: LineSegment StartX=4e-16 StartY=-43.35 StartZ=0 EndX=2.90119 EndY=-41.675 EndZ=0
    g119: LineSegment StartX=2.90119 StartY=-41.675 StartZ=0 EndX=2.90119 EndY=-38.325 EndZ=0
    g120: LineSegment StartX=2.90119 StartY=-38.325 StartZ=0 EndX=0 EndY=-36.65 EndZ=0
    g121: Circle CenterX=0 CenterY=-40 CenterZ=0 NormalX=0 NormalY=0 NormalZ=1 AngleXU=0 Radius=3.35
    g122: LineSegment StartX=0 StartY=-16.65 StartZ=0 EndX=-2.90119 EndY=-18.325 EndZ=0
    g123: LineSegment StartX=-2.90119 StartY=-18.325 StartZ=0 EndX=-2.90119 EndY=-21.675 EndZ=0
    g124: LineSegment StartX=-2.90119 StartY=-21.675 StartZ=0 EndX=-4e-16 EndY=-23.35 EndZ=0
    g125: LineSegment StartX=-4e-16 StartY=-23.35 StartZ=0 EndX=2.90119 EndY=-21.675 EndZ=0
    g126: LineSegment StartX=2.90119 StartY=-21.675 StartZ=0 EndX=2.90119 EndY=-18.325 EndZ=0
    g127: LineSegment StartX=2.90119 StartY=-18.325 StartZ=0 EndX=0 EndY=-16.65 EndZ=0
    g128: Circle CenterX=0 CenterY=-20 CenterZ=0 NormalX=0 NormalY=0 NormalZ=1 AngleXU=0 Radius=3.35
    g129: LineSegment StartX=65 StartY=-156.65 StartZ=0 EndX=62.0988 EndY=-158.325 EndZ=0
    g130: LineSegment StartX=62.0988 StartY=-158.325 StartZ=0 EndX=62.0988 EndY=-161.675 EndZ=0
    g131: LineSegment StartX=62.0988 StartY=-161.675 StartZ=0 EndX=65 EndY=-163.35 EndZ=0
    g132: LineSegment StartX=65 StartY=-163.35 StartZ=0 EndX=67.9012 EndY=-161.675 EndZ=0
    g133: LineSegment StartX=67.9012 StartY=-161.675 StartZ=0 EndX=67.9012 EndY=-158.325 EndZ=0
    g134: LineSegment StartX=67.9012 StartY=-158.325 StartZ=0 EndX=65 EndY=-156.65 EndZ=0
    g135: Circle CenterX=65 CenterY=-160 CenterZ=0 NormalX=0 NormalY=0 NormalZ=1 AngleXU=0 Radius=3.35
    g136: LineSegment StartX=65 StartY=-136.65 StartZ=0 EndX=62.0988 EndY=-138.325 EndZ=0
    g137: LineSegment StartX=62.0988 StartY=-138.325 StartZ=0 EndX=62.0988 EndY=-141.675 EndZ=0
    g138: LineSegment StartX=62.0988 StartY=-141.675 StartZ=0 EndX=65 EndY=-143.35 EndZ=0
    g139: LineSegment StartX=65 StartY=-143.35 StartZ=0 EndX=67.9012 EndY=-141.675 EndZ=0
    g140: LineSegment StartX=67.9012 StartY=-141.675 StartZ=0 EndX=67.9012 EndY=-138.325 EndZ=0
    g141: LineSegment StartX=67.9012 StartY=-138.325 StartZ=0 EndX=65 EndY=-136.65 EndZ=0
    g142: Circle CenterX=65 CenterY=-140 CenterZ=0 NormalX=0 NormalY=0 NormalZ=1 AngleXU=0 Radius=3.35
    g143: LineSegment StartX=65 StartY=-116.65 StartZ=0 EndX=62.0988 EndY=-118.325 EndZ=0
    g144: LineSegment StartX=62.0988 StartY=-118.325 StartZ=0 EndX=62.0988 EndY=-121.675 EndZ=0
    g145: LineSegment StartX=62.0988 StartY=-121.675 StartZ=0 EndX=65 EndY=-123.35 EndZ=0
    g146: LineSegment StartX=65 StartY=-123.35 StartZ=0 EndX=67.9012 EndY=-121.675 EndZ=0
    g147: LineSegment StartX=67.9012 StartY=-121.675 StartZ=0 EndX=67.9012 EndY=-118.325 EndZ=0
    g148: LineSegment StartX=67.9012 StartY=-118.325 StartZ=0 EndX=65 EndY=-116.65 EndZ=0
    g149: Circle CenterX=65 CenterY=-120 CenterZ=0 NormalX=0 NormalY=0 NormalZ=1 AngleXU=0 Radius=3.35
    g150: LineSegment StartX=65 StartY=-96.65 StartZ=0 EndX=62.0988 EndY=-98.325 EndZ=0
    g151: LineSegment StartX=62.0988 StartY=-98.325 StartZ=0 EndX=62.0988 EndY=-101.675 EndZ=0
    g152: LineSegment StartX=62.0988 StartY=-101.675 StartZ=0 EndX=65 EndY=-103.35 EndZ=0
    g153: LineSegment StartX=65 StartY=-103.35 StartZ=0 EndX=67.9012 EndY=-101.675 EndZ=0
    g154: LineSegment StartX=67.9012 StartY=-101.675 StartZ=0 EndX=67.9012 EndY=-98.325 EndZ=0
    g155: LineSegment StartX=67.9012 StartY=-98.325 StartZ=0 EndX=65 EndY=-96.65 EndZ=0
    g156: Circle CenterX=65 CenterY=-100 CenterZ=0 NormalX=0 NormalY=0 NormalZ=1 AngleXU=0 Radius=3.35
    g157: LineSegment StartX=65 StartY=-76.65 StartZ=0 EndX=62.0988 EndY=-78.325 EndZ=0
    g158: LineSegment StartX=62.0988 StartY=-78.325 StartZ=0 EndX=62.0988 EndY=-81.675 EndZ=0
    g159: LineSegment StartX=62.0988 StartY=-81.675 StartZ=0 EndX=65 EndY=-83.35 EndZ=0
    g160: LineSegment StartX=65 StartY=-83.35 StartZ=0 EndX=67.9012 EndY=-81.675 EndZ=0
    g161: LineSegment StartX=67.9012 StartY=-81.675 StartZ=0 EndX=67.9012 EndY=-78.325 EndZ=0
    g162: LineSegment StartX=67.9012 StartY=-78.325 StartZ=0 EndX=65 EndY=-76.65 EndZ=0
    g163: Circle CenterX=65 CenterY=-80 CenterZ=0 NormalX=0 NormalY=0 NormalZ=1 AngleXU=0 Radius=3.35
    g164: LineSegment StartX=65 StartY=-56.65 StartZ=0 EndX=62.0988 EndY=-58.325 EndZ=0
    g165: LineSegment StartX=62.0988 StartY=-58.325 StartZ=0 EndX=62.0988 EndY=-61.675 EndZ=0
    g166: LineSegment StartX=62.0988 StartY=-61.675 StartZ=0 EndX=65 EndY=-63.35 EndZ=0
    g167: LineSegment StartX=65 StartY=-63.35 StartZ=0 EndX=67.9012 EndY=-61.675 EndZ=0
    g168: LineSegment StartX=67.9012 StartY=-61.675 StartZ=0 EndX=67.9012 EndY=-58.325 EndZ=0
    g169: LineSegment StartX=67.9012 StartY=-58.325 StartZ=0 EndX=65 EndY=-56.65 EndZ=0
    g170: Circle CenterX=65 CenterY=-60 CenterZ=0 NormalX=0 NormalY=0 NormalZ=1 AngleXU=0 Radius=3.35
    g171: LineSegment StartX=65 StartY=-36.65 StartZ=0 EndX=62.0988 EndY=-38.325 EndZ=0
    g172: LineSegment StartX=62.0988 StartY=-38.325 StartZ=0 EndX=62.0988 EndY=-41.675 EndZ=0
    g173: LineSegment StartX=62.0988 StartY=-41.675 StartZ=0 EndX=65 EndY=-43.35 EndZ=0
    g174: LineSegment StartX=65 StartY=-43.35 StartZ=0 EndX=67.9012 EndY=-41.675 EndZ=0
    g175: LineSegment StartX=67.9012 StartY=-41.675 StartZ=0 EndX=67.9012 EndY=-38.325 EndZ=0
    g176: LineSegment StartX=67.9012 StartY=-38.325 StartZ=0 EndX=65 EndY=-36.65 EndZ=0
    g177: Circle CenterX=65 CenterY=-40 CenterZ=0 NormalX=0 NormalY=0 NormalZ=1 AngleXU=0 Radius=3.35
    g178: LineSegment StartX=65 StartY=-16.65 StartZ=0 EndX=62.0988 EndY=-18.325 EndZ=0
    g179: LineSegment StartX=62.0988 StartY=-18.325 StartZ=0 EndX=62.0988 EndY=-21.675 EndZ=0
    g180: LineSegment StartX=62.0988 StartY=-21.675 StartZ=0 EndX=65 EndY=-23.35 EndZ=0
    g181: LineSegment StartX=65 StartY=-23.35 StartZ=0 EndX=67.9012 EndY=-21.675 EndZ=0
    g182: LineSegment StartX=67.9012 StartY=-21.675 StartZ=0 EndX=67.9012 EndY=-18.325 EndZ=0
    g183: LineSegment StartX=67.9012 StartY=-18.325 StartZ=0 EndX=65 EndY=-16.65 EndZ=0
    g184: Circle CenterX=65 CenterY=-20 CenterZ=0 NormalX=0 NormalY=0 NormalZ=1 AngleXU=0 Radius=3.35
  constraints (453):
    c: Symmetric(g0,g0,g-2)
    c: DistanceY(g0) = -160
    c: PointOnObject(g1,g-1)
    c: PointOnObject(g1,g0)
    c: Vertical(g1)
    c: PointOnObject(g2,g-1)
    c: Vertical(g2)
    c: Symmetric(g1,g2,g-2)
    c: DistanceX(g1,g2) = 130
    c: Coincident(g0,g4)
    c: Coincident(g3,g4)
    c: Distance(g4) = 20
    c: Angle(g4) = 1.5708
    c: Coincident(g3,g6)
    c: Coincident(g5,g6)
    c: Equal(g4,g6)
    c: Parallel(g6,g4)
    c: Coincident(g5,g8)
    c: Coincident(g7,g8)
    c: Equal(g4,g8)
    c: Parallel(g8,g4)
    c: Coincident(g7,g10)
    c: Coincident(g9,g10)
    c: Equal(g4,g10)
    c: Parallel(g10,g4)
    c: Coincident(g9,g12)
    c: Coincident(g11,g12)
    c: Equal(g4,g12)
    c: Parallel(g12,g4)
    c: Coincident(g11,g14)
    c: Coincident(g13,g14)
    c: Equal(g4,g14)
    c: Parallel(g14,g4)
    c: Coincident(g13,g16)
    c: Coincident(g15,g16)
    c: Equal(g4,g16)
    c: Parallel(g16,g4)
    c: Symmetric(g3,g3,g-2)
    c: Symmetric(g5,g5,g-2)
    c: Symmetric(g7,g7,g-2)
    c: Symmetric(g9,g9,g-2)
    c: Symmetric(g11,g11,g-2)
    c: Symmetric(g13,g13,g-2)
    c: Symmetric(g15,g15,g-2)
    c: DistanceX(g0) = -150
    c: Coincident(g17,g18)
    c: Coincident(g18,g19)
    c: Coincident(g19,g20)
    c: Coincident(g20,g21)
    c: Coincident(g21,g22)
    c: Coincident(g22,g17)
    c: Equal(g17, g18-g22) x5
    c: PointOnObject(g17,g23)
    c: PointOnObject(g18,g23)
    c: PointOnObject(g19,g23)
    c: PointOnObject(g20,g23)
    c: PointOnObject(g21,g23)
    c: PointOnObject(g22,g23)
    c: PointOnObject(g23,g1)
    c: PointOnObject(g22,g1)
    c: Coincident(g24,g25)
    c: Coincident(g25,g26)
    c: Coincident(g26,g27)
    c: Coincident(g27,g28)
    c: Coincident(g28,g29)
    c: Coincident(g29,g24)
    c: Equal(g24, g25-g29) x5
    c: PointOnObject(g24,g30)
    c: PointOnObject(g25,g30)
    c: PointOnObject(g26,g30)
    c: PointOnObject(g27,g30)
    c: PointOnObject(g28,g30)
    c: PointOnObject(g29,g30)
    c: PointOnObject(g30,g1)
    c: PointOnObject(g29,g1)
    c: Coincident(g31,g32)
    c: Coincident(g32,g33)
    c: Coincident(g33,g34)
    c: Coincident(g34,g35)
    c: Coincident(g35,g36)
    c: Coincident(g36,g31)
    c: Equal(g31, g32-g36) x5
    c: PointOnObject(g31,g37)
    c: PointOnObject(g32,g37)
    c: PointOnObject(g33,g37)
    c: PointOnObject(g34,g37)
    c: PointOnObject(g35,g37)
    c: PointOnObject(g36,g37)
    c: PointOnObject(g37,g1)
    c: PointOnObject(g36,g1)
    c: Coincident(g38,g39)
    c: Coincident(g39,g40)
    c: Coincident(g40,g41)
    c: Coincident(g41,g42)
    c: Coincident(g42,g43)
    c: Coincident(g43,g38)
    c: Equal(g38, g39-g43) x5
    c: PointOnObject(g38,g44)
    c: PointOnObject(g39,g44)
    c: PointOnObject(g40,g44)
    c: PointOnObject(g41,g44)
    c: PointOnObject(g42,g44)
    c: PointOnObject(g43,g44)
    c: PointOnObject(g44,g1)
    c: PointOnObject(g43,g1)
    c: Coincident(g45,g46)
    c: Coincident(g46,g47)
    c: Coincident(g47,g48)
    c: Coincident(g48,g49)
    c: Coincident(g49,g50)
    c: Coincident(g50,g45)
    c: Equal(g45, g46-g50) x5
    c: PointOnObject(g45,g51)
    c: PointOnObject(g46,g51)
    c: PointOnObject(g47,g51)
    c: PointOnObject(g48,g51)
    c: PointOnObject(g49,g51)
    c: PointOnObject(g50,g51)
    c: PointOnObject(g51,g1)
    c: PointOnObject(g50,g1)
    c: Coincident(g52,g53)
    c: Coincident(g53,g54)
    c: Coincident(g54,g55)
    c: Coincident(g55,g56)
    c: Coincident(g56,g57)
    c: Coincident(g57,g52)
    c: Equal(g52, g53-g57) x5
    c: PointOnObject(g52,g58)
    c: PointOnObject(g53,g58)
    c: PointOnObject(g54,g58)
    c: PointOnObject(g55,g58)
    c: PointOnObject(g56,g58)
    c: PointOnObject(g57,g58)
    c: PointOnObject(g58,g1)
    c: PointOnObject(g57,g1)
    c: Coincident(g59,g60)
    c: Coincident(g60,g61)
    c: Coincident(g61,g62)
    c: Coincident(g62,g63)
    c: Coincident(g63,g64)
    c: Coincident(g64,g59)
    c: Equal(g59, g60-g64) x5
    c: PointOnObject(g59,g65)
    c: PointOnObject(g60,g65)
    c: PointOnObject(g61,g65)
    c: PointOnObject(g62,g65)
    c: PointOnObject(g63,g65)
    c: PointOnObject(g64,g65)
    c: PointOnObject(g65,g1)
    c: PointOnObject(g64,g1)
    c: Coincident(g66,g67)
    c: Coincident(g67,g68)
    c: Coincident(g68,g69)
    c: Coincident(g69,g70)
    c: Coincident(g70,g71)
    c: Coincident(g71,g66)
    c: Equal(g66, g67-g71) x5
    c: PointOnObject(g66,g72)
    c: PointOnObject(g67,g72)
    c: PointOnObject(g68,g72)
    c: PointOnObject(g69,g72)
    c: PointOnObject(g70,g72)
    c: PointOnObject(g71,g72)
    c: PointOnObject(g72,g1)
    c: PointOnObject(g71,g1)
    c: Coincident(g73,g74)
    c: Coincident(g74,g75)
    c: Coincident(g75,g76)
    c: Coincident(g76,g77)
    c: Coincident(g77,g78)
    c: Coincident(g78,g73)
    c: Equal(g73, g74-g78) x5
    c: PointOnObject(g73,g79)
    c: PointOnObject(g74,g79)
    c: PointOnObject(g75,g79)
    c: PointOnObject(g76,g79)
    c: PointOnObject(g77,g79)
    c: PointOnObject(g78,g79)
    c: PointOnObject(g79,g-2)
    c: PointOnObject(g78,g-2)
    c: Coincident(g80,g81)
    c: Coincident(g81,g82)
    c: Coincident(g82,g83)
    c: Coincident(g83,g84)
    c: Coincident(g84,g85)
    c: Coincident(g85,g80)
    c: Equal(g80, g81-g85) x5
    c: PointOnObject(g80,g86)
    c: PointOnObject(g81,g86)
    c: PointOnObject(g82,g86)
    c: PointOnObject(g83,g86)
    c: PointOnObject(g84,g86)
    c: PointOnObject(g85,g86)
    c: PointOnObject(g86,g-2)
    c: PointOnObject(g85,g-2)
    c: Coincident(g87,g88)
    c: Coincident(g88,g89)
    c: Coincident(g89,g90)
    c: Coincident(g90,g91)
    c: Coincident(g91,g92)
    c: Coincident(g92,g87)
    c: Equal(g87, g88-g92) x5
    c: PointOnObject(g87,g93)
    c: PointOnObject(g88,g93)
    c: PointOnObject(g89,g93)
    c: PointOnObject(g90,g93)
    c: PointOnObject(g91,g93)
    c: PointOnObject(g92,g93)
    c: PointOnObject(g93,g-2)
    c: PointOnObject(g92,g-2)
    c: Coincident(g94,g95)
    c: Coincident(g95,g96)
    c: Coincident(g96,g97)
    c: Coincident(g97,g98)
    c: Coincident(g98,g99)
    c: Coincident(g99,g94)
    c: Equal(g94, g95-g99) x5
    c: PointOnObject(g94,g100)
    c: PointOnObject(g95,g100)
    c: PointOnObject(g96,g100)
    c: PointOnObject(g97,g100)
    c: PointOnObject(g98,g100)
    c: PointOnObject(g99,g100)
    c: PointOnObject(g100,g-2)
    c: PointOnObject(g99,g-2)
    c: Coincident(g101,g102)
    c: Coincident(g102,g103)
    c: Coincident(g103,g104)
    c: Coincident(g104,g105)
    c: Coincident(g105,g106)
    c: Coincident(g106,g101)
    c: Equal(g101, g102-g106) x5
    c: PointOnObject(g101,g107)
    c: PointOnObject(g102,g107)
    c: PointOnObject(g103,g107)
    c: PointOnObject(g104,g107)
    c: PointOnObject(g105,g107)
    c: PointOnObject(g106,g107)
    c: PointOnObject(g107,g-2)
    c: PointOnObject(g106,g-2)
    c: Coincident(g108,g109)
    c: Coincident(g109,g110)
    c: Coincident(g110,g111)
    c: Coincident(g111,g112)
    c: Coincident(g112,g113)
    c: Coincident(g113,g108)
    c: Equal(g108, g109-g113) x5
    c: PointOnObject(g108,g114)
    c: PointOnObject(g109,g114)
    c: PointOnObject(g110,g114)
    c: PointOnObject(g111,g114)
    c: PointOnObject(g112,g114)
    c: PointOnObject(g113,g114)
    c: PointOnObject(g114,g-2)
    c: PointOnObject(g113,g-2)
    c: Coincident(g115,g116)
    c: Coincident(g116,g117)
    c: Coincident(g117,g118)
    c: Coincident(g118,g119)
    c: Coincident(g119,g120)
    c: Coincident(g120,g115)
    c: Equal(g115, g116-g120) x5
    c: PointOnObject(g115,g121)
    c: PointOnObject(g116,g121)
    c: PointOnObject(g117,g121)
    c: PointOnObject(g118,g121)
    c: PointOnObject(g119,g121)
    c: PointOnObject(g120,g121)
    c: PointOnObject(g121,g-2)
    c: PointOnObject(g120,g-2)
    c: Coincident(g122,g123)
    c: Coincident(g123,g124)
    c: Coincident(g124,g125)
    c: Coincident(g125,g126)
    c: Coincident(g126,g127)
    c: Coincident(g127,g122)
    c: Equal(g122, g123-g127) x5
    c: PointOnObject(g122,g128)
    c: PointOnObject(g123,g128)
    c: PointOnObject(g124,g128)
    c: PointOnObject(g125,g128)
    c: PointOnObject(g126,g128)
    c: PointOnObject(g127,g128)
    c: PointOnObject(g128,g-2)
    c: PointOnObject(g127,g-2)
    c: Coincident(g129,g130)
    c: Coincident(g130,g131)
    c: Coincident(g131,g132)
    c: Coincident(g132,g133)
    c: Coincident(g133,g134)
    c: Coincident(g134,g129)
    c: Equal(g129, g130-g134) x5
    c: PointOnObject(g129,g135)
    c: PointOnObject(g130,g135)
    c: PointOnObject(g131,g135)
    c: PointOnObject(g132,g135)
    c: PointOnObject(g133,g135)
    c: PointOnObject(g134,g135)
    c: PointOnObject(g135,g2)
    c: PointOnObject(g134,g2)
    c: Coincident(g136,g137)
    c: Coincident(g137,g138)
    c: Coincident(g138,g139)
    c: Coincident(g139,g140)
    c: Coincident(g140,g141)
    c: Coincident(g141,g136)
    c: Equal(g136, g137-g141) x5
    c: PointOnObject(g136,g142)
    c: PointOnObject(g137,g142)
    c: PointOnObject(g138,g142)
    c: PointOnObject(g139,g142)
    c: PointOnObject(g140,g142)
    c: PointOnObject(g141,g142)
    c: PointOnObject(g142,g2)
    c: PointOnObject(g141,g2)
    c: Coincident(g143,g144)
    c: Coincident(g144,g145)
    c: Coincident(g145,g146)
    c: Coincident(g146,g147)
    c: Coincident(g147,g148)
    c: Coincident(g148,g143)
    c: Equal(g143, g144-g148) x5
    c: PointOnObject(g143,g149)
    c: PointOnObject(g144,g149)
    c: PointOnObject(g145,g149)
    c: PointOnObject(g146,g149)
    c: PointOnObject(g147,g149)
    c: PointOnObject(g148,g149)
    c: PointOnObject(g149,g2)
    c: PointOnObject(g148,g2)
    c: Coincident(g150,g151)
    c: Coincident(g151,g152)
    c: Coincident(g152,g153)
    c: Coincident(g153,g154)
    c: Coincident(g154,g155)
    c: Coincident(g155,g150)
    c: Equal(g150, g151-g155) x5
    c: PointOnObject(g150,g156)
    c: PointOnObject(g151,g156)
    c: PointOnObject(g152,g156)
    c: PointOnObject(g153,g156)
    c: PointOnObject(g154,g156)
    c: PointOnObject(g155,g156)
    c: PointOnObject(g156,g2)
    c: PointOnObject(g155,g2)
    c: Coincident(g157,g158)
    c: Coincident(g158,g159)
    c: Coincident(g159,g160)
    c: Coincident(g160,g161)
    c: Coincident(g161,g162)
    c: Coincident(g162,g157)
    c: Equal(g157, g158-g162) x5
    c: PointOnObject(g157,g163)
    c: PointOnObject(g158,g163)
    c: PointOnObject(g159,g163)
    c: PointOnObject(g160,g163)
    c: PointOnObject(g161,g163)
    c: PointOnObject(g162,g163)
    c: PointOnObject(g163,g2)
    c: PointOnObject(g162,g2)
    c: Coincident(g164,g165)
    c: Coincident(g165,g166)
    c: Coincident(g166,g167)
    c: Coincident(g167,g168)
    c: Coincident(g168,g169)
    c: Coincident(g169,g164)
    c: Equal(g164, g165-g169) x5
    c: PointOnObject(g164,g170)
    c: PointOnObject(g165,g170)
    c: PointOnObject(g166,g170)
    c: PointOnObject(g167,g170)
    c: PointOnObject(g168,g170)
    c: PointOnObject(g169,g170)
    c: PointOnObject(g170,g2)
    c: PointOnObject(g169,g2)
    c: Coincident(g171,g172)
    c: Coincident(g172,g173)
    c: Coincident(g173,g174)
    c: Coincident(g174,g175)
    c: Coincident(g175,g176)
    c: Coincident(g176,g171)
    c: Equal(g171, g172-g176) x5
    c: PointOnObject(g171,g177)
    c: PointOnObject(g172,g177)
    c: PointOnObject(g173,g177)
    c: PointOnObject(g174,g177)
    c: PointOnObject(g175,g177)
    c: PointOnObject(g176,g177)
    c: PointOnObject(g177,g2)
    c: PointOnObject(g176,g2)
    c: Coincident(g178,g179)
    c: Coincident(g179,g180)
    c: Coincident(g180,g181)
    c: Coincident(g181,g182)
    c: Coincident(g182,g183)
    c: Coincident(g183,g178)
    c: Equal(g178, g179-g183) x5
    c: PointOnObject(g178,g184)
    c: PointOnObject(g179,g184)
    c: PointOnObject(g180,g184)
    c: PointOnObject(g181,g184)
    c: PointOnObject(g182,g184)
    c: PointOnObject(g183,g184)
    c: PointOnObject(g184,g2)
    c: PointOnObject(g183,g2)
    c: Radius(g23) = 3.35
    c: PointOnObject(g23,g0)
    c: PointOnObject(g30,g3)
    c: PointOnObject(g37,g5)
    c: PointOnObject(g44,g7)
    c: PointOnObject(g51,g9)
    c: PointOnObject(g58,g11)
    c: PointOnObject(g65,g13)
    c: PointOnObject(g72,g15)
    c: PointOnObject(g79,g0)
    c: PointOnObject(g86,g3)
    c: PointOnObject(g93,g5)
    c: PointOnObject(g100,g7)
    c: PointOnObject(g107,g9)
    c: PointOnObject(g114,g11)
    c: PointOnObject(g121,g13)
    c: PointOnObject(g128,g15)
    c: PointOnObject(g135,g0)
    c: PointOnObject(g142,g3)
    c: PointOnObject(g149,g5)
    c: PointOnObject(g156,g7)
    c: PointOnObject(g163,g9)
    c: PointOnObject(g170,g11)
    c: PointOnObject(g177,g13)
    c: PointOnObject(g184,g15)
    c: Radius(g30) = 3.35
    c: Radius(g37) = 3.35
    c: Radius(g44) = 3.35
    c: Radius(g51) = 3.35
    c: Radius(g58) = 3.35
    c: Radius(g65) = 3.35
    c: Radius(g72) = 3.35
    c: Radius(g79) = 3.35
    c: Radius(g86) = 3.35
    c: Radius(g93) = 3.35
    c: Radius(g100) = 3.35
    c: Radius(g107) = 3.35
    c: Radius(g114) = 3.35
    c: Radius(g121) = 3.35
    c: Radius(g128) = 3.35
    c: Radius(g135) = 3.35
    c: Radius(g142) = 3.35
    c: Radius(g149) = 3.35
    c: Radius(g156) = 3.35
    c: Radius(g163) = 3.35
    c: Radius(g170) = 3.35
    c: Radius(g177) = 3.35
    c: Radius(g184) = 3.35
FEATURE [PartDesign::Pocket] Pocket038
  BaseFeature = -> Hole035
  Direction = (0,0,-1)
  Length = 6
  Length2 = 5
  Profile = -> Sketch099
  ReferenceAxis = -> Sketch099 [N_Axis]
  Reversed = true
  Type = 0
FEATURE [PartDesign::Body] Body005  label="RearPanelPlate"
  Group = -> [Sketch089,Pad033,Binder009,Hole034,Sketch097,Hole035,Sketch099,Pocket038]
  Origin = -> Origin012
  Tip = -> Pocket038
COMPONENT P9 — recipe-attached ("RightPanel", modeled in this document).
Construction recipe (the document's own serialized feature program — sketch geometry with constraints, then the solid features built on it; lengths are millimeters unless a unit is written):

FEATURE [Sketcher::SketchObject] Sketch026
  FullyConstrained = true
  MapMode = 5
  Placement = pos=(0,0,0) rot=(0.57735,0.57735,0.57735;2.0944rad)
  Support = -> [YZ_Plane015]
  expr: Constraints[16] = <<Variables>>.WallThickness
  expr: Constraints[19] = -<<Variables>>.WallThickness
  expr: Constraints[56] = <<Variables>>.WallThickness
  expr: Constraints[57] = <<Variables>>.GantorySpacing + <<Variables>>.CavitySpacingY * 2
  sketch-geometry (25):
    g0: LineSegment StartX=-110 StartY=15 StartZ=0 EndX=-115 EndY=15 EndZ=0
    g1: LineSegment StartX=-117 StartY=13 StartZ=0 EndX=-115 EndY=15 EndZ=0
    g2: LineSegment StartX=-117 StartY=13 StartZ=0 EndX=-117 EndY=-2 EndZ=0
    g3: LineSegment StartX=-117 StartY=-2 StartZ=0 EndX=-112 EndY=-7 EndZ=0
    g4: LineSegment StartX=-112 StartY=-7 StartZ=0 EndX=112 EndY=-7 EndZ=0
    g5: LineSegment StartX=112 StartY=-7 StartZ=0 EndX=117 EndY=-2 EndZ=0
    g6: LineSegment StartX=117 StartY=-2 StartZ=0 EndX=117 EndY=10 EndZ=0
    g7: LineSegment StartX=117 StartY=10 StartZ=0 EndX=105 EndY=10 EndZ=0
    g8: LineSegment StartX=-110 StartY=10 StartZ=0 EndX=-110 EndY=15 EndZ=0
    g9: LineSegment StartX=-40 StartY=0 StartZ=0 EndX=-95 EndY=0 EndZ=0
    g10: LineSegment StartX=-33 StartY=7 StartZ=0 EndX=-40 EndY=0 EndZ=0
    g11: LineSegment StartX=-29.5 StartY=7 StartZ=0 EndX=-33 EndY=7 EndZ=0
    g12: LineSegment StartX=-2 StartY=0 StartZ=0 EndX=-28 EndY=0 EndZ=0
    g13: LineSegment StartX=3 StartY=7 StartZ=0 EndX=-0.5 EndY=7 EndZ=0
    g14: LineSegment StartX=10 StartY=0 StartZ=0 EndX=3 EndY=7 EndZ=0
    g15: LineSegment StartX=-95 StartY=0 StartZ=0 EndX=-105 EndY=10 EndZ=0
    g16: LineSegment StartX=-105 StartY=10 StartZ=0 EndX=-110 EndY=10 EndZ=0
    g17: LineSegment StartX=-28 StartY=0 StartZ=0 EndX=-28 EndY=5.5 EndZ=0
    g18: LineSegment StartX=-28 StartY=5.5 StartZ=0 EndX=-29.5 EndY=7 EndZ=0
    g19: LineSegment StartX=-0.5 StartY=7 StartZ=0 EndX=-2 EndY=5.5 EndZ=0
    g20: LineSegment StartX=-2 StartY=5.5 StartZ=0 EndX=-2 EndY=0 EndZ=0
    g21: LineSegment StartX=105 StartY=10 StartZ=0 EndX=95 EndY=0 EndZ=0
    g22: LineSegment StartX=95 StartY=0 StartZ=0 EndX=10 EndY=0 EndZ=0
    g23: GeomPoint X=110 Y=10 Z=0
    g24: LineSegment StartX=-15 StartY=60 StartZ=0 EndX=-15 EndY=-60 EndZ=0
  constraints (66):
    c: Coincident(g9,g15)
    c: Coincident(g8,g0)
    c: Horizontal(g0)
    c: Vertical(g2)
    c: Coincident(g2,g3)
    c: Coincident(g3,g4)
    c: Coincident(g4,g5)
    c: Coincident(g5,g6)
    c: Vertical(g6)
    c: Coincident(g6,g7)
    c: Horizontal(g7)
    c: Angle(g5) = 0.785398
    c: Angle(g3) = -0.785398
    c: Angle(g1) = 0.785398
    c: Coincident(g0,g1)
    c: Coincident(g2,g1)
    c: DistanceX(g1,g8) = 7
    c: DistanceX(g1,g1) = 2
    c: DistanceX(g3,g3) = 5
    c: DistanceY(g3) = -7
    c: DistanceY(g0) = 15
    c: DistanceY(g6) = 10
    c: Coincident(g16,g8)
    c: Vertical(g8)
    c: Coincident(g10,g9)
    c: Coincident(g11,g10)
    c: Coincident(g18,g11)
    c: Coincident(g12,g17)
    c: Coincident(g20,g12)
    c: Coincident(g13,g19)
    c: Coincident(g14,g13)
    c: Coincident(g22,g14)
    c: Coincident(g15,g16)
    c: Parallel(g15,g3)
    c: Coincident(g17,g18)
    c: Coincident(g19,g20)
    c: Coincident(g21,g7)
    c: Coincident(g21,g22)
    c: Symmetric(g9,g21,g-2)
    c: Symmetric(g15,g7,g-2)
    c: Horizontal(g16)
    c: PointOnObject(g9,g-1)
    c: PointOnObject(g9,g-1)
    c: PointOnObject(g12,g-1)
    c: Parallel(g10,g1)
    c: Horizontal(g11)
    c: Vertical(g17)
    c: Parallel(g18,g3)
    c: DistanceX(g12,g12) = 26
    c: DistanceX(g11,g17) = 1.5
    c: DistanceX(g10,g17) = 5
    c: DistanceY(g10) = 7
    c: DistanceX(g16,g16) = 5
    c: Symmetric(g4,g3,g-2)
    c: Symmetric(g2,g5,g-2)
    c: PointOnObject(g23,g7)
    c: DistanceX(g23,g6) = 7
    c: DistanceX(g8,g23) = 220
    c: Symmetric(g24,g24,g-1)
    c: DistanceX(g24) = -15
    c: DistanceY(g24) = -60
    c: Symmetric(g12,g12,g24)
    c: Symmetric(g17,g19,g24)
    c: Symmetric(g11,g13,g24)
    c: Symmetric(g10,g13,g24)
    c: Symmetric(g9,g14,g24)
FEATURE [Sketcher::SketchObject] Sketch029
  AttachmentOffset = pos=(0,0,-185) rot=(0,0,1;0rad)
  FullyConstrained = true
  MapMode = 5
  Placement = pos=(-185,4.11e-14,-4.11e-14) rot=(0.57735,0.57735,0.57735;2.0944rad)
  Support = -> [YZ_Plane015]
  expr: Constraints[1] = <<Variables>>.GantorySpacing
  sketch-geometry (6):
    g0: ArcOfCircle CenterX=-100 CenterY=10 CenterZ=0 NormalX=0 NormalY=0 NormalZ=1 AngleXU=0 Radius=15 StartAngle=0 EndAngle=1.5708
    g1: ArcOfCircle CenterX=100 CenterY=10 CenterZ=0 NormalX=0 NormalY=0 NormalZ=1 AngleXU=0 Radius=15 StartAngle=1.5708 EndAngle=3.14159
    g2: LineSegment StartX=-100 StartY=25 StartZ=0 EndX=-100 EndY=10 EndZ=0
    g3: LineSegment StartX=-100 StartY=10 StartZ=0 EndX=-85 EndY=10 EndZ=0
    g4: LineSegment StartX=85 StartY=10 StartZ=0 EndX=100 EndY=10 EndZ=0
    g5: LineSegment StartX=100 StartY=25 StartZ=0 EndX=100 EndY=10 EndZ=0
  constraints (17):
    c: Symmetric(g0,g1,g-2)
    c: DistanceX(g0,g1) = 200
    c: DistanceY(g0) = 10
    c: Coincident(g0,g2)
    c: Coincident(g3,g2)
    c: Coincident(g0,g3)
    c: Coincident(g1,g5)
    c: Coincident(g1,g4)
    c: Coincident(g4,g5)
    c: Equal(g0,g1)
    c: Diameter(g0) = 30
    c: Symmetric(g2,g4,g-2)
    c: Vertical(g2)
    c: Horizontal(g3)
    c: Coincident(g2,g0)
    c: Vertical(g5)
    c: Horizontal(g4)
FEATURE [Sketcher::SketchObject] Sketch035
  FullyConstrained = true
  MapMode = 5
  Support = -> [XY_Plane015]
  expr: Constraints[10] = <<Variables>>.GantorySpacing + <<Variables>>.CavitySpacingY * 2
  expr: Constraints[14] = <<Variables>>.PullyDiameterDrive + <<Variables>>.PullyDiameterIdler
  sketch-geometry (28):
    g0: LineSegment StartX=-25 StartY=110 StartZ=0 EndX=-10 EndY=95 EndZ=0
    g1: LineSegment StartX=-10 StartY=95 StartZ=0 EndX=-10 EndY=-95 EndZ=0
    g2: LineSegment StartX=0 StartY=-110 StartZ=0 EndX=0 EndY=110 EndZ=0
    g3: LineSegment StartX=0 StartY=110 StartZ=0 EndX=-25 EndY=110 EndZ=0
    g4: LineSegment StartX=-25 StartY=-110 StartZ=0 EndX=-10 EndY=-95 EndZ=0
    g5: LineSegment StartX=0 StartY=-110 StartZ=0 EndX=-25 EndY=-110 EndZ=0
    g6: Circle CenterX=-5 CenterY=-2.27 CenterZ=0 NormalX=0 NormalY=0 NormalZ=1 AngleXU=0 Radius=1.25
    g7: Circle CenterX=-5 CenterY=-27.73 CenterZ=0 NormalX=0 NormalY=0 NormalZ=1 AngleXU=0 Radius=1.25
    g8: LineSegment StartX=-100 StartY=110 StartZ=0 EndX=-100 EndY=-110 EndZ=0
    g9: LineSegment StartX=-190 StartY=75 StartZ=0 EndX=-155 EndY=110 EndZ=0
    g10: LineSegment StartX=-155 StartY=110 StartZ=0 EndX=-200 EndY=110 EndZ=0
    g11: LineSegment StartX=-200 StartY=110 StartZ=0 EndX=-200 EndY=8.63871 EndZ=0
    g12: LineSegment StartX=-200 StartY=-110 StartZ=0 EndX=-155 EndY=-110 EndZ=0
    g13: LineSegment StartX=-155 StartY=-110 StartZ=0 EndX=-190 EndY=-75 EndZ=0
    g14: GeomPoint X=-195 Y=-27.73 Z=0
    g15: ArcOfCircle CenterX=-195 CenterY=-2.27 CenterZ=0 NormalX=0 NormalY=0 NormalZ=1 AngleXU=0 Radius=12 StartAngle=5.27493 EndAngle=7.29145
    g16: ArcOfCircle CenterX=-187 CenterY=10.4186 CenterZ=0 NormalX=0 NormalY=0 NormalZ=1 AngleXU=0 Radius=3 StartAngle=3.14159 EndAngle=4.14985
    g17: ArcOfCircle CenterX=-187 CenterY=-14.9586 CenterZ=0 NormalX=0 NormalY=0 NormalZ=1 AngleXU=0 Radius=3 StartAngle=2.13333 EndAngle=3.14159
    g18: LineSegment StartX=-190 StartY=-75 StartZ=0 EndX=-190 EndY=-14.9586 EndZ=0
    g19: LineSegment StartX=-190 StartY=10.4186 StartZ=0 EndX=-190 EndY=75 EndZ=0
    g20: LineSegment StartX=-200 StartY=-13.1787 StartZ=0 EndX=-200 EndY=-110 EndZ=0
    g21: ArcOfCircle CenterX=-195 CenterY=-2.27 CenterZ=0 NormalX=0 NormalY=0 NormalZ=1 AngleXU=0 Radius=12 StartAngle=2.00057 EndAngle=4.28261
    g22: GeomPoint X=-195 Y=-2.27 Z=0
    g23: LineSegment StartX=-188.5 StartY=-20 StartZ=0 EndX=-11.5 EndY=-20 EndZ=0
    g24: LineSegment StartX=-11.5 StartY=-20 StartZ=0 EndX=-11.5 EndY=-10 EndZ=0
    g25: LineSegment StartX=-11.5 StartY=-10 StartZ=0 EndX=-188.5 EndY=-10 EndZ=0
    g26: LineSegment StartX=-188.5 StartY=-10 StartZ=0 EndX=-188.5 EndY=-20 EndZ=0
    g27: LineSegment StartX=-200 StartY=-15 StartZ=0 EndX=0 EndY=-15 EndZ=0
  constraints (67):
    c: Coincident(g0,g1)
    c: PointOnObject(g2,g-2)
    c: Coincident(g2,g3)
    c: Coincident(g3,g0)
    c: Horizontal(g3)
    c: Coincident(g5,g4)
    c: Angle(g0) = -0.785398
    c: Symmetric(g5,g2,g-1)
    c: Symmetric(g0,g4,g-1)
    c: Symmetric(g0,g4,g-1)
    c: DistanceY(g5,g2) = 220
    c: DistanceX(g1) = -10
    c: DistanceX(g0,g0) = 15
    c: DistanceX(g6) = -5
    c: DistanceY(g7,g6) = 25.46
    c: Equal(g6,g7)
    c: Diameter(g6) = 2.5
    c: Coincident(g2,g5)
    c: Coincident(g1,g4)
    c: Symmetric(g8,g8,g-1)
    c: DistanceX(g8) = -100
    c: PointOnObject(g8,g3)
    c: Coincident(g9,g10)
    c: Coincident(g10,g11)
    c: Coincident(g20,g12)
    c: Coincident(g12,g13)
    c: Coincident(g13,g18)
    c: Coincident(g19,g9)
    c: Symmetric(g10,g2,g8)
    c: Symmetric(g20,g2,g8)
    c: Symmetric(g14,g7,g8)
    c: Tangent(g15,g16) = 1.5708
    c: Tangent(g16,g19) = 1.5708
    c: Diameter(g16) = 6
    c: Diameter(g15) = 24
    c: Vertical(g19)
    c: Vertical(g18)
    c: Coincident(g11,g21)
    c: Coincident(g20,g21)
    c: Diameter(g21) = 24
    c: Vertical(g20)
    c: Vertical(g11)
    c: Coincident(g22,g15)
    c: Symmetric(g15,g6,g8)
    c: Coincident(g22,g21)
    c: Coincident(g23,g24)
    c: Coincident(g24,g25)
    c: Coincident(g25,g26)
    c: Coincident(g26,g23)
    c: Symmetric(g25,g24,g8)
    c: DistanceY(g26,g26) = 10
    c: DistanceX(g25,g25) = 177
    c: Tangent(g17,g18) = 1.5708
    c: Equal(g17,g16)
    c: DistanceX(g10,g9) = 10
    c: Parallel(g13,g0)
    c: Symmetric(g13,g9,g-1)
    c: Symmetric(g9,g12,g-1)
    c: Horizontal(g10)
    c: DistanceX(g9,g9) = 35
    c: Tangent(g15,g17) = 1.5708
    c: Symmetric(g27,g27,g8)
    c: PointOnObject(g27,g-2)
    c: DistanceY(g27) = -15
    c: Symmetric(g6,g7,g27)
    c: Symmetric(g25,g23,g27)
    c: Symmetric(g24,g23,g27)
FEATURE [Sketcher::SketchObject] Sketch039
  AttachmentOffset = pos=(0,0,10) rot=(0,0,1;0rad)
  FullyConstrained = true
  MapMode = 5
  Placement = pos=(0,0,10) rot=(0,0,1;0rad)
  Support = -> [XY_Plane015]
  expr: .AttachmentOffset.Base.z = Variables.CavitySpacingX
  expr: Constraints[1] = <<Variables>>.PullyDiameterDrive + <<Variables>>.PullyDiameterIdler
  sketch-geometry (4):
    g0: GeomPoint X=-195 Y=-27.73 Z=0
    g1: GeomPoint X=-195 Y=-2.27 Z=0
    g2: Circle CenterX=-195 CenterY=-2.27 CenterZ=0 NormalX=0 NormalY=0 NormalZ=1 AngleXU=0 Radius=8
    g3: LineSegment StartX=0 StartY=-15 StartZ=0 EndX=-250 EndY=-15 EndZ=0
  constraints (9):
    c: DistanceX(g1) = -195
    c: DistanceY(g0,g1) = 25.46
    c: Coincident(g2,g1)
    c: Diameter(g2) = 16
    c: PointOnObject(g3,g-2)
    c: Horizontal(g3)
    c: DistanceX(g3,g3) = 250
    c: DistanceY(g3) = -15
    c: Symmetric(g2,g0,g3)
FEATURE [Sketcher::SketchObject] Sketch069
  FullyConstrained = true
  MapMode = 5
  Placement = pos=(0,0,0) rot=(1,0,0;1.5708rad)
  Support = -> [XZ_Plane015]
  sketch-geometry (13):
    g0: LineSegment StartX=-210 StartY=40 StartZ=0 EndX=-200 EndY=40 EndZ=0
    g1: LineSegment StartX=0 StartY=-0.2 StartZ=0 EndX=-210 EndY=-0.2 EndZ=0
    g2: LineSegment StartX=-210 StartY=-0.2 StartZ=0 EndX=-210 EndY=40 EndZ=0
    g3: LineSegment StartX=-200 StartY=40 StartZ=0 EndX=-171.757 EndY=11.7574 EndZ=0
    g4: LineSegment StartX=-167.515 StartY=10 StartZ=0 EndX=-190 EndY=10 EndZ=0
    g5: LineSegment StartX=-190 StartY=10 StartZ=0 EndX=-190 EndY=5 EndZ=0
    g6: LineSegment StartX=-190 StartY=5 StartZ=0 EndX=-185 EndY=0 EndZ=0
    g7: ArcOfCircle CenterX=-167.515 CenterY=16 CenterZ=0 NormalX=0 NormalY=0 NormalZ=1 AngleXU=0 Radius=6 StartAngle=3.92699 EndAngle=4.71239
    g8: LineSegment StartX=0 StartY=-0.2 StartZ=0 EndX=0 EndY=10 EndZ=0
    g9: LineSegment StartX=0 StartY=10 StartZ=0 EndX=-10 EndY=10 EndZ=0
    g10: LineSegment StartX=-10 StartY=10 StartZ=0 EndX=-10 EndY=8 EndZ=0
    g11: LineSegment StartX=-18 StartY=0 StartZ=0 EndX=-10 EndY=8 EndZ=0
    g12: LineSegment StartX=-18 StartY=0 StartZ=0 EndX=-185 EndY=0 EndZ=0
  constraints (38):
    c: Coincident(g0,g3)
    c: Horizontal(g1)
    c: Coincident(g2,g0)
    c: Horizontal(g0)
    c: Vertical(g2)
    c: DistanceY(g0) = 40
    c: Coincident(g2,g1)
    c: PointOnObject(g6,g-1)
    c: DistanceX(g0,g0) = 10
    c: DistanceX(g1) = -210
    c: Coincident(g4,g5)
    c: Coincident(g5,g6)
    c: Horizontal(g4)
    c: Vertical(g5)
    c: Angle(g3) = -0.785398
    c: Parallel(g3,g6)
    c: DistanceY(g4) = 10
    c: DistanceY(g5) = 5
    c: DistanceX(g1,g4) = 20
    c: Tangent(g7,g3) = -1.5708
    c: Tangent(g7,g4) = 1.5708
    c: Diameter(g7) = 12
    c: DistanceY(g1) = -0.2
    c: Coincident(g8,g9)
    c: Horizontal(g9)
    c: Coincident(g9,g10)
    c: Vertical(g10)
    c: Coincident(g8,g1)
    c: PointOnObject(g1,g-2)
    c: PointOnObject(g8,g-2)
    c: Coincident(g12,g6)
    c: Horizontal(g12)
    c: Angle(g11) = 0.785398
    c: Coincident(g11,g12)
    c: Coincident(g11,g10)
    c: DistanceY(g10) = 8
    c: DistanceY(g8) = 10
    c: DistanceX(g9) = -10
FEATURE [Sketcher::SketchObject] Sketch072
  FullyConstrained = true
  MapMode = 5
  Support = -> [XY_Plane015]
  sketch-geometry (6):
    g0: LineSegment StartX=-188.5 StartY=-9.5 StartZ=0 EndX=-11.5 EndY=-9.5 EndZ=0
    g1: LineSegment StartX=-11.5 StartY=-9.5 StartZ=0 EndX=-11.5 EndY=-20.5 EndZ=0
    g2: LineSegment StartX=-11.5 StartY=-20.5 StartZ=0 EndX=-188.5 EndY=-20.5 EndZ=0
    g3: LineSegment StartX=-188.5 StartY=-20.5 StartZ=0 EndX=-188.5 EndY=-9.5 EndZ=0
    g4: GeomPoint X=-100 Y=-15 Z=0
    g5: LineSegment StartX=0 StartY=-15 StartZ=0 EndX=-250 EndY=-15 EndZ=0
  constraints (15):
    c: Coincident(g0,g1)
    c: Coincident(g1,g2)
    c: Coincident(g2,g3)
    c: Coincident(g3,g0)
    c: Horizontal(g0)
    c: DistanceX(g0,g0) = 177
    c: DistanceY(g3,g3) = 11
    c: Symmetric(g0,g1,g4)
    c: DistanceX(g4) = -100
    c: PointOnObject(g5,g-2)
    c: Horizontal(g5)
    c: DistanceX(g5) = -250
    c: DistanceY(g5) = -15
    c: Symmetric(g0,g1,g5)
    c: Symmetric(g0,g2,g5)
FEATURE [Sketcher::SketchObject] Sketch077
  FullyConstrained = true
  MapMode = 5
  Support = -> [XY_Plane015]
  expr: Constraints[21] = <<Variables>>.GantorySpacing + Variables.WallThickness * 2 + 16 - 40 - 20
  sketch-geometry (12):
    g0: LineSegment StartX=26 StartY=85 StartZ=0 EndX=154 EndY=85 EndZ=0
    g1: LineSegment StartX=160 StartY=79 StartZ=0 EndX=160 EndY=-79 EndZ=0
    g2: LineSegment StartX=154 StartY=-85 StartZ=0 EndX=26 EndY=-85 EndZ=0
    g3: LineSegment StartX=20 StartY=-79 StartZ=0 EndX=20 EndY=79 EndZ=0
    g4: ArcOfCircle CenterX=26 CenterY=79 CenterZ=0 NormalX=0 NormalY=0 NormalZ=1 AngleXU=0 Radius=6 StartAngle=1.5708 EndAngle=3.14159
    g5: GeomPoint X=20 Y=85 Z=0
    g6: ArcOfCircle CenterX=26 CenterY=-79 CenterZ=0 NormalX=0 NormalY=0 NormalZ=1 AngleXU=0 Radius=6 StartAngle=3.14159 EndAngle=4.71239
    g7: GeomPoint X=20 Y=-85 Z=0
    g8: ArcOfCircle CenterX=154 CenterY=-79 CenterZ=0 NormalX=0 NormalY=0 NormalZ=1 AngleXU=0 Radius=6 StartAngle=4.71239 EndAngle=6.28319
    g9: GeomPoint X=160 Y=-85 Z=0
    g10: ArcOfCircle CenterX=154 CenterY=79 CenterZ=0 NormalX=0 NormalY=0 NormalZ=1 AngleXU=0 Radius=6 StartAngle=-9e-16 EndAngle=1.5708
    g11: GeomPoint X=160 Y=85 Z=0
  constraints (26):
    c: DistanceX(g7,g9) = 140
    c: PointOnObject(g5,g0)
    c: PointOnObject(g5,g3)
    c: Tangent(g0,g4) = 1.5708
    c: Tangent(g3,g4) = 1.5708
    c: PointOnObject(g7,g3)
    c: PointOnObject(g7,g2)
    c: Tangent(g3,g6) = 1.5708
    c: Tangent(g2,g6) = 1.5708
    c: PointOnObject(g9,g1)
    c: PointOnObject(g9,g2)
    c: Tangent(g1,g8) = 1.5708
    c: Tangent(g2,g8) = 1.5708
    c: PointOnObject(g11,g0)
    c: PointOnObject(g11,g1)
    c: Tangent(g0,g10) = 1.5708
    c: Tangent(g1,g10) = 1.5708
    c: Equal(g4,g6)
    c: Equal(g4,g8)
    c: Equal(g4,g10)
    c: Radius(g4) = 6
    c: DistanceY(g7,g5) = 170
    c: Symmetric(g7,g5,g-1)
    c: Symmetric(g11,g9,g-1)
    c: Horizontal(g0)
    c: DistanceX(g7) = 20
FEATURE [Sketcher::SketchObject] Sketch112
  FullyConstrained = true
  MapMode = 5
  Placement = pos=(0,0,0) rot=(1,0,0;1.5708rad)
  Support = -> [XZ_Plane015]
  expr: Constraints[8] = -<<Variables>>.WallThickness
  sketch-geometry (3):
    g0: LineSegment StartX=-210 StartY=13 StartZ=0 EndX=-190 EndY=-7 EndZ=0
    g1: LineSegment StartX=-190 StartY=-7 StartZ=0 EndX=-210 EndY=-7 EndZ=0
    g2: LineSegment StartX=-210 StartY=-7 StartZ=0 EndX=-210 EndY=13 EndZ=0
  constraints (9):
    c: Horizontal(g1)
    c: Coincident(g1,g2)
    c: Coincident(g2,g0)
    c: Angle(g0) = -0.785398
    c: DistanceX(g0) = -190
    c: Vertical(g2)
    c: DistanceX(g1,g1) = 20
    c: Coincident(g1,g0)
    c: DistanceY(g0) = -7
FEATURE [PartDesign::Pad] Pad048  label="Pad RightPanel UnderFrame"
  Direction = (0,-1,-2e-16)
  Length = 220
  Length2 = 10
  Midplane = true
  Placement = pos=(0,0,0) rot=(1,0,0;1.5708rad)
  Profile = -> Sketch069
  ReferenceAxis = -> Sketch069 [N_Axis]
  Type = 0
  expr: Length = <<Variables>>.GantorySpacing + <<Variables>>.CavitySpacingY * 2
FEATURE [Sketcher::SketchObject] Sketch114
  AttachmentOffset = pos=(0,0,10) rot=(0,0,1;0rad)
  FullyConstrained = true
  MapMode = 5
  Placement = pos=(0,0,10) rot=(0,0,1;0rad)
  Support = -> [XY_Plane015]
  expr: Constraints[5] = <<Variables>>.GantorySpacing
  sketch-geometry (8):
    g0: LineSegment StartX=0 StartY=100 StartZ=0 EndX=-190 EndY=100 EndZ=0
    g1: LineSegment StartX=-200 StartY=90 StartZ=0 EndX=-200 EndY=-90 EndZ=0
    g2: LineSegment StartX=-190 StartY=-100 StartZ=0 EndX=0 EndY=-100 EndZ=0
    g3: LineSegment StartX=0 StartY=-100 StartZ=0 EndX=0 EndY=100 EndZ=0
    g4: ArcOfCircle CenterX=-190 CenterY=90 CenterZ=0 NormalX=0 NormalY=0 NormalZ=1 AngleXU=0 Radius=10 StartAngle=1.5708 EndAngle=3.14159
    g5: GeomPoint X=-200 Y=100 Z=0
    g6: ArcOfCircle CenterX=-190 CenterY=-90 CenterZ=0 NormalX=0 NormalY=0 NormalZ=1 AngleXU=0 Radius=10 StartAngle=3.14159 EndAngle=4.71239
    g7: GeomPoint X=-200 Y=-100 Z=0
  constraints (18):
    c: Coincident(g2,g3)
    c: Coincident(g3,g0)
    c: Horizontal(g0)
    c: PointOnObject(g0,g-2)
    c: Symmetric(g0,g2,g-1)
    c: DistanceY(g2,g0) = 200
    c: Symmetric(g7,g5,g-1)
    c: PointOnObject(g5,g0)
    c: PointOnObject(g5,g1)
    c: Tangent(g0,g4) = -1.5708
    c: Tangent(g1,g4) = -1.5708
    c: PointOnObject(g7,g1)
    c: PointOnObject(g7,g2)
    c: Tangent(g1,g6) = -1.5708
    c: Tangent(g2,g6) = -1.5708
    c: Equal(g4,g6)
    c: Diameter(g4) = 20
    c: DistanceX(g5) = -200
FEATURE [PartDesign::Pocket] Pocket046  label="Pocket RightPanel UnderFrameCut"
  BaseFeature = -> Pad048
  Direction = (0,0,-1)
  Length = 5
  Length2 = 5
  Placement = pos=(0,0,0) rot=(1,0,0;1.5708rad)
  Profile = -> Sketch114
  ReferenceAxis = -> Sketch114 [N_Axis]
  Reversed = true
  Type = 1
FEATURE [Sketcher::SketchObject] Sketch115
  FullyConstrained = true
  MapMode = 5
  Placement = pos=(0,0,0) rot=(1,0,0;1.5708rad)
  Support = -> [XZ_Plane015]
  sketch-geometry (5):
    g0: LineSegment StartX=-190 StartY=0 StartZ=0 EndX=-210 EndY=0 EndZ=0
    g1: LineSegment StartX=-210 StartY=0 StartZ=0 EndX=-210 EndY=20 EndZ=0
    g2: ArcOfCircle CenterX=-190 CenterY=20 CenterZ=0 NormalX=0 NormalY=0 NormalZ=1 AngleXU=0 Radius=10 StartAngle=3.14159 EndAngle=4.71239
    g3: LineSegment StartX=-210 StartY=20 StartZ=0 EndX=-200 EndY=20 EndZ=0
    g4: LineSegment StartX=-190 StartY=10 StartZ=0 EndX=-190 EndY=0 EndZ=0
  constraints (16):
    c: Horizontal(g0)
    c: Coincident(g0,g1)
    c: Vertical(g1)
    c: PointOnObject(g0,g-1)
    c: DistanceX(g0) = -210
    c: DistanceY(g1) = 20
    c: Coincident(g3,g1)
    c: Horizontal(g3)
    c: Coincident(g3,g2)
    c: DistanceX(g3,g3) = 10
    c: Coincident(g4,g2)
    c: Vertical(g4)
    c: Coincident(g4,g0)
    c: DistanceY(g4,g4) = 10
    c: DistanceX(g0,g0) = 20
    c: Diameter(g2) = 20
FEATURE [PartDesign::Pad] Pad050  label="Pad RightPanel UnderFrameFillet"
  BaseFeature = -> Pocket046
  Direction = (0,-1,-2e-16)
  Length = 220
  Length2 = 10
  Midplane = true
  Placement = pos=(0,0,0) rot=(1,0,0;1.5708rad)
  Profile = -> Sketch115
  ReferenceAxis = -> Sketch115 [N_Axis]
  Type = 0
  expr: Length = <<Variables>>.GantorySpacing + <<Variables>>.CavitySpacingY * 2
FEATURE [PartDesign::Pad] Pad032  label="Pad RightPanel Plate"
  BaseFeature = -> Pad050
  Direction = (1,-2e-16,3e-16)
  Length = 210
  Length2 = 10
  Placement = pos=(0,0,0) rot=(1,0,0;1.5708rad)
  Profile = -> Sketch026
  ReferenceAxis = -> Sketch026 [N_Axis]
  Reversed = true
  Type = 0
FEATURE [PartDesign::Pad] Pad046  label="Pad RightPanel Frame"
  BaseFeature = -> Pad032
  Direction = (0,0,1)
  Length = 10
  Length2 = 10
  Placement = pos=(0,0,0) rot=(1,0,0;1.5708rad)
  Profile = -> Sketch035
  ReferenceAxis = -> Sketch035 [N_Axis]
  Type = 0
FEATURE [Sketcher::SketchObject] Sketch116
  AttachmentOffset = pos=(0,0,-210) rot=(0,0,1;0rad)
  FullyConstrained = true
  MapMode = 5
  Placement = pos=(-210,4.66e-14,-4.66e-14) rot=(0.57735,0.57735,0.57735;2.0944rad)
  Support = -> [YZ_Plane015]
  expr: Constraints[1] = <<Variables>>.GantorySpacing
  expr: Constraints[2] = <<Variables>>.CavitySpacingX
  sketch-geometry (2):
    g0: Circle CenterX=-100 CenterY=10 CenterZ=0 NormalX=0 NormalY=0 NormalZ=1 AngleXU=0 Radius=10
    g1: Circle CenterX=100 CenterY=10 CenterZ=0 NormalX=0 NormalY=0 NormalZ=1 AngleXU=0 Radius=10
  constraints (5):
    c: Symmetric(g0,g1,g-2)
    c: DistanceX(g0,g1) = 200
    c: DistanceY(g0) = 10
    c: Equal(g0,g1)
    c: Diameter(g0) = 20
FEATURE [Sketcher::SketchObject] Sketch121
  FullyConstrained = true
  MapMode = 5
  Support = -> [XY_Plane015]
  expr: Constraints[0] = Sketch039.Constraints[0]
  expr: Constraints[1] = Sketch039.Constraints[1]
  expr: Constraints[6] = Sketch039.Constraints[6]
  expr: Constraints[7] = Sketch039.Constraints[7]
  sketch-geometry (4):
    g0: GeomPoint X=-195 Y=-27.73 Z=0
    g1: GeomPoint X=-195 Y=-2.27 Z=0
    g2: Circle CenterX=-195 CenterY=-2.27 CenterZ=0 NormalX=0 NormalY=0 NormalZ=1 AngleXU=0 Radius=12
    g3: LineSegment StartX=0 StartY=-15 StartZ=0 EndX=-250 EndY=-15 EndZ=0
  constraints (9):
    c: DistanceX(g1) = -195
    c: DistanceY(g0,g1) = 25.46
    c: Coincident(g2,g1)
    c: Diameter(g2) = 24
    c: PointOnObject(g3,g-2)
    c: Horizontal(g3)
    c: DistanceX(g3,g3) = 250
    c: DistanceY(g3) = -15
    c: Symmetric(g2,g0,g3)
FEATURE [PartDesign::Pad] Pad053  label="Pad RightPanel BearingHold"
  BaseFeature = -> Pad046
  Direction = (0,0,1)
  Length = 15
  Length2 = 10
  Placement = pos=(0,0,0) rot=(1,0,0;1.5708rad)
  Profile = -> Sketch121
  ReferenceAxis = -> Sketch121 [N_Axis]
  Type = 0
  expr: Length = Variables.CavitySpacingX + 5
FEATURE [PartDesign::Pocket] Pocket035  label="Pocket RightPanel BearingHole"
  BaseFeature = -> Pad053
  Direction = (0,0,-1)
  Length = 10
  Length2 = 5
  Placement = pos=(0,0,0) rot=(1,0,0;1.5708rad)
  Profile = -> Sketch039
  ReferenceAxis = -> Sketch039 [N_Axis]
  Reversed = true
  Type = 1
FEATURE [Sketcher::SketchObject] Sketch122
  AttachmentOffset = pos=(0,0,5) rot=(0,0,1;0rad)
  FullyConstrained = true
  MapMode = 5
  Placement = pos=(0,0,5) rot=(0,0,1;0rad)
  Support = -> [XY_Plane015]
  expr: .AttachmentOffset.Base.z = Variables.CavitySpacingX - 5
  expr: Constraints[0] = Sketch039.Constraints[0]
  expr: Constraints[1] = Sketch039.Constraints[1]
  expr: Constraints[6] = Sketch039.Constraints[6]
  expr: Constraints[7] = Sketch039.Constraints[7]
  sketch-geometry (4):
    g0: GeomPoint X=-195 Y=-27.73 Z=0
    g1: GeomPoint X=-195 Y=-2.27 Z=0
    g2: Circle CenterX=-195 CenterY=-2.27 CenterZ=0 NormalX=0 NormalY=0 NormalZ=1 AngleXU=0 Radius=4
    g3: LineSegment StartX=0 StartY=-15 StartZ=0 EndX=-250 EndY=-15 EndZ=0
  constraints (9):
    c: DistanceX(g1) = -195
    c: DistanceY(g0,g1) = 25.46
    c: Coincident(g2,g1)
    c: Diameter(g2) = 8
    c: PointOnObject(g3,g-2)
    c: Horizontal(g3)
    c: DistanceX(g3,g3) = 250
    c: DistanceY(g3) = -15
    c: Symmetric(g2,g0,g3)
FEATURE [PartDesign::Pocket] Pocket048  label="Pocket RightPanel ShaftHole"
  BaseFeature = -> Pocket035
  Direction = (0,0,-1)
  Length = 5
  Length2 = 5
  Placement = pos=(0,0,0) rot=(1,0,0;1.5708rad)
  Profile = -> Sketch122
  ReferenceAxis = -> Sketch122 [N_Axis]
  Reversed = true
  Type = 1
FEATURE [Sketcher::SketchObject] Sketch123
  AttachmentOffset = pos=(0,0,15) rot=(0,0,1;0rad)
  FullyConstrained = true
  MapMode = 5
  Placement = pos=(0,0,15) rot=(0,0,1;0rad)
  Support = -> [XY_Plane015]
  expr: .AttachmentOffset.Base.z = Variables.CavitySpacingX + 5
  expr: Constraints[0] = Sketch039.Constraints[0]
  expr: Constraints[1] = Sketch039.Constraints[1]
  expr: Constraints[6] = Sketch039.Constraints[6]
  expr: Constraints[7] = Sketch039.Constraints[7]
  sketch-geometry (4):
    g0: GeomPoint X=-195 Y=-27.73 Z=0
    g1: GeomPoint X=-195 Y=-2.27 Z=0
    g2: Circle CenterX=-195 CenterY=-2.27 CenterZ=0 NormalX=0 NormalY=0 NormalZ=1 AngleXU=0 Radius=9
    g3: LineSegment StartX=0 StartY=-15 StartZ=0 EndX=-250 EndY=-15 EndZ=0
  constraints (9):
    c: DistanceX(g1) = -195
    c: DistanceY(g0,g1) = 25.46
    c: Coincident(g2,g1)
    c: Diameter(g2) = 18
    c: PointOnObject(g3,g-2)
    c: Horizontal(g3)
    c: DistanceX(g3,g3) = 250
    c: DistanceY(g3) = -15
    c: Symmetric(g2,g0,g3)
FEATURE [PartDesign::Pocket] Pocket049  label="Pocket RightPanel PullyHole"
  BaseFeature = -> Pocket048
  Direction = (0,0,-1)
  Length = 5
  Length2 = 5
  Placement = pos=(0,0,0) rot=(1,0,0;1.5708rad)
  Profile = -> Sketch123
  ReferenceAxis = -> Sketch123 [N_Axis]
  Reversed = true
  Type = 1
FEATURE [PartDesign::Pocket] Pocket023  label="Pocket RightPanel Rail"
  BaseFeature = -> Pocket049
  Direction = (0,0,-1)
  Length = 200
  Length2 = 5
  Placement = pos=(0,0,0) rot=(1,0,0;1.5708rad)
  Profile = -> Sketch072
  ReferenceAxis = -> Sketch072 [N_Axis]
  Reversed = true
  Type = 1
FEATURE [PartDesign::Pad] Pad049  label="Pad RightPanel FootHold"
  BaseFeature = -> Pocket023
  Direction = (1,-2e-16,3e-16)
  Length = 25
  Length2 = 10
  Placement = pos=(0,0,0) rot=(1,0,0;1.5708rad)
  Profile = -> Sketch029
  ReferenceAxis = -> Sketch029 [N_Axis]
  Reversed = true
  Type = 0
FEATURE [PartDesign::Pocket] Pocket047  label="Pocket RightPanel FootHole"
  BaseFeature = -> Pad049
  Direction = (-1,2e-16,-3e-16)
  Length = 10
  Length2 = 5
  Placement = pos=(0,0,0) rot=(1,0,0;1.5708rad)
  Profile = -> Sketch116
  ReferenceAxis = -> Sketch116 [N_Axis]
  Reversed = true
  Type = 0
FEATURE [PartDesign::Pocket] Pocket045  label="Pocket RightPanel UnderCut"
  BaseFeature = -> Pocket047
  Direction = (0,1,2e-16)
  Length = 5
  Length2 = 5
  Midplane = true
  Placement = pos=(0,0,0) rot=(1,0,0;1.5708rad)
  Profile = -> Sketch112
  ReferenceAxis = -> Sketch112 [N_Axis]
  Type = 1
FEATURE [PartDesign::Boolean] Boolean005  label="Boolean RightPanel Kumiko"
  BaseFeature = -> Pocket045
  Group = -> [Body019]
  Refine = true
  Type = 0
FEATURE [PartDesign::Pocket] Pocket024  label="Pocket RightPanel Window"
  BaseFeature = -> Boolean005
  Direction = (0,0,-1)
  Length = 5
  Length2 = 5
  Midplane = true
  Profile = -> Sketch077
  ReferenceAxis = -> Sketch077 [N_Axis]
  Type = 1
FEATURE [PartDesign::Body] Body006  label="RightPanelPlate"
  Group = -> [Pad048,Pocket046,Pad050,Pad032,Pad046,Pad053,Pocket035,Pocket048,Pocket049,Sketch069,Pocket023,Sketch039,Sketch072,Sketch077,Sketch112,Sketch026,Sketch029,Sketch035,Pad049,Pocket047,Pocket045,Sketch123,Boolean005,Pocket024,Sketch115,Sketch114,Sketch116,Sketch121,Sketch122]
  Origin = -> Origin015
  Tip = -> Pocket045
COMPONENT P10 — recipe-attached ("BottomPanel", modeled in this document).
Construction recipe (the document's own serialized feature program — sketch geometry with constraints, then the solid features built on it; lengths are millimeters unless a unit is written):

FEATURE [Sketcher::SketchObject] Sketch113
  FullyConstrained = true
  MapMode = 5
  Placement = pos=(0,0,0) rot=(1,0,0;1.5708rad)
  Support = -> [XZ_Plane018]
  sketch-geometry (4):
    g0: LineSegment StartX=-95 StartY=10 StartZ=0 EndX=95 EndY=10 EndZ=0
    g1: LineSegment StartX=95 StartY=10 StartZ=0 EndX=95 EndY=0 EndZ=0
    g2: LineSegment StartX=95 StartY=0 StartZ=0 EndX=-95 EndY=0 EndZ=0
    g3: LineSegment StartX=-95 StartY=0 StartZ=0 EndX=-95 EndY=10 EndZ=0
  constraints (10):
    c: Coincident(g0,g1)
    c: Coincident(g1,g2)
    c: Coincident(g2,g3)
    c: Coincident(g3,g0)
    c: Symmetric(g0,g0,g-2)
    c: Symmetric(g2,g1,g-2)
    c: Vertical(g3)
    c: PointOnObject(g2,g-1)
    c: DistanceY(g3,g3) = 10
    c: DistanceX(g2,g2) = 190
FEATURE [PartDesign::Pad] Pad047
  Direction = (0,-1,-2e-16)
  Length = 234
  Length2 = 10
  Midplane = true
  Placement = pos=(0,0,0) rot=(1,0,0;1.5708rad)
  Profile = -> Sketch113
  ReferenceAxis = -> Sketch113 [N_Axis]
  Type = 0
  expr: Length = <<Variables>>.GantorySpacing + (<<Variables>>.CavitySpacingY + <<Variables>>.WallThickness) * 2
FEATURE [PartDesign::Body] Body008  label="BottomPanelPlate"
  Group = -> [Sketch113,Pad047]
  Origin = -> Origin018
  Tip = -> Pad047
COMPONENT P11 — recipe-attached ("FrontPanel", modeled in this document).
Construction recipe (the document's own serialized feature program — sketch geometry with constraints, then the solid features built on it; lengths are millimeters unless a unit is written):

FEATURE [PartDesign::AdditiveBox] Box037
  AttacherType = Attacher::AttachEngine3D
  AttachmentOffset = pos=(-95,-5,0) rot=(0,0,1;0rad)
  Height = 30
  Length = 190
  MapMode = 5
  Placement = pos=(-95,-5,0) rot=(0,0,1;0rad)
  Support = -> [XY_Plane020]
  Width = 5
  expr: .AttachmentOffset.Base.x = -(<<Variables>>.GantorySpacing - 10) / 2
  expr: .AttachmentOffset.Base.y = -(<<Variables>>.WallThickness - 2)
  expr: Length = <<Variables>>.GantorySpacing - 10
  expr: Width = <<Variables>>.WallThickness - 2
FEATURE [Sketcher::SketchObject] Sketch063
  FullyConstrained = true
  MapMode = 5
  Placement = pos=(0,0,0) rot=(1,0,0;1.5708rad)
  Support = -> [XZ_Plane020]
  expr: Constraints[7] = <<Variables>>.GantorySpacing - 20
  sketch-geometry (6):
    g0: Circle CenterX=-90 CenterY=25 CenterZ=0 NormalX=0 NormalY=0 NormalZ=1 AngleXU=0 Radius=1.5
    g1: Circle CenterX=-90 CenterY=5 CenterZ=0 NormalX=0 NormalY=0 NormalZ=1 AngleXU=0 Radius=1.5
    g2: Circle CenterX=-35 CenterY=15 CenterZ=0 NormalX=0 NormalY=0 NormalZ=1 AngleXU=0 Radius=1.5
    g3: Circle CenterX=35 CenterY=15 CenterZ=0 NormalX=0 NormalY=0 NormalZ=1 AngleXU=0 Radius=1.5
    g4: Circle CenterX=90 CenterY=25 CenterZ=0 NormalX=0 NormalY=0 NormalZ=1 AngleXU=0 Radius=1.5
    g5: Circle CenterX=90 CenterY=5 CenterZ=0 NormalX=0 NormalY=0 NormalZ=1 AngleXU=0 Radius=1.5
  constraints (11):
    c: Vertical(g1,g0)
    c: Symmetric(g0,g4,g-2)
    c: Symmetric(g1,g5,g-2)
    c: Symmetric(g2,g3,g-2)
    c: DistanceY(g2) = 15
    c: DistanceY(g1) = 5
    c: DistanceY(g0) = 25
    c: DistanceX(g1,g5) = 180
    c: DistanceX(g2,g3) = 70
    c: Equal(g0, g1-g5) x5
    c: Diameter(g0) = 3
FEATURE [PartDesign::Hole] Hole024
  BaseFeature = -> Box037
  CustomThreadClearance = 0
  Depth = 396.347
  DepthType = 1
  Diameter = 3.4
  DrillForDepth = false
  DrillPoint = 1
  DrillPointAngle = 118
  HoleCutCountersinkAngle = 90
  HoleCutCustomValues = false
  HoleCutDepth = 0
  HoleCutDiameter = 6.1
  HoleCutType = 0
  ModelThread = false
  Placement = pos=(-95,-5,0) rot=(0,0,1;0rad)
  Profile = -> Sketch063
  Reversed = true
  Tapered = false
  TaperedAngle = 90
  ThreadClass = 0
  ThreadDepth = 396.347
  ThreadDepthType = 0
  ThreadDirection = 0
  ThreadFit = 0
  ThreadSize = 9
  ThreadType = 1
  Threaded = false
  UseCustomThreadClearance = false
FEATURE [PartDesign::Body] Body009  label="FrontPanelPlate"
  Group = -> [Box037,Sketch063,Hole024]
  Origin = -> Origin020
  Tip = -> Hole024
COMPONENT P12 — recipe-attached ("Hat", modeled in this document).
Construction recipe (the document's own serialized feature program — sketch geometry with constraints, then the solid features built on it; lengths are millimeters unless a unit is written):

FEATURE [Sketcher::SketchObject] Sketch017
  FullyConstrained = true
  MapMode = 5
  Placement = pos=(0,0,0) rot=(0.57735,0.57735,0.57735;2.0944rad)
  Support = -> [YZ_Plane022]
  expr: Constraints[15] = <<Variables>>.GantorySpacing - 30
  expr: Constraints[8] = <<Variables>>.GantorySpacing - 10
  expr: Constraints[9] = <<Variables>>.GantorySpacing - 30
  sketch-geometry (8):
    g0: LineSegment StartX=-85 StartY=60 StartZ=0 EndX=85 EndY=60 EndZ=0
    g1: LineSegment StartX=85 StartY=60 StartZ=0 EndX=95 EndY=0 EndZ=0
    g2: LineSegment StartX=95 StartY=0 StartZ=0 EndX=85 EndY=0 EndZ=0
    g3: LineSegment StartX=-95 StartY=0 StartZ=0 EndX=-85 EndY=60 EndZ=0
    g4: LineSegment StartX=-85 StartY=0 StartZ=0 EndX=-76.6667 EndY=50 EndZ=0
    g5: LineSegment StartX=-76.6667 StartY=50 StartZ=0 EndX=76.6667 EndY=50 EndZ=0
    g6: LineSegment StartX=76.6667 StartY=50 StartZ=0 EndX=85 EndY=0 EndZ=0
    g7: LineSegment StartX=-85 StartY=0 StartZ=0 EndX=-95 EndY=0 EndZ=0
  constraints (20):
    c: Coincident(g0,g1)
    c: Coincident(g1,g2)
    c: Coincident(g7,g3)
    c: Coincident(g3,g0)
    c: PointOnObject(g1,g-1)
    c: Symmetric(g0,g0,g-2)
    c: Symmetric(g7,g1,g-2)
    c: DistanceY(g-1,g0) = 60
    c: DistanceX(g7,g1) = 190
    c: DistanceX(g0,g0) = 170
    c: Coincident(g5,g4)
    c: Coincident(g6,g5)
    c: Symmetric(g4,g5,g-2)
    c: Symmetric(g4,g6,g-2)
    c: Parallel(g4,g3)
    c: DistanceX(g4,g6) = 170
    c: DistanceY(g-1,g4) = 50
    c: Coincident(g7,g4)
    c: Coincident(g2,g6)
    c: PointOnObject(g4,g-1)
FEATURE [PartDesign::Pad] Pad005
  Direction = (1,-2e-16,3e-16)
  Length = 220
  Length2 = 10
  Midplane = true
  Placement = pos=(0,0,0) rot=(0.57735,0.57735,0.57735;2.0944rad)
  Profile = -> Sketch017
  ReferenceAxis = -> Sketch017 [N_Axis]
  Type = 0
  expr: Length = <<Variables>>.GantorySpacing + 20
FEATURE [Sketcher::SketchObject] Sketch018
  FullyConstrained = true
  MapMode = 5
  Placement = pos=(0,0,0) rot=(1,0,0;1.5708rad)
  Support = -> [XZ_Plane022]
  expr: Constraints[26] = <<Variables>>.GantorySpacing + 20
  expr: Constraints[28] = <<Variables>>.GantorySpacing
  expr: Constraints[7] = <<Variables>>.GantorySpacing - 20
  sketch-geometry (12):
    g0: LineSegment StartX=-90 StartY=50 StartZ=0 EndX=90 EndY=50 EndZ=0
    g1: LineSegment StartX=90 StartY=50 StartZ=0 EndX=98.3333 EndY=0 EndZ=0
    g2: LineSegment StartX=98.3333 StartY=0 StartZ=0 EndX=-98.3333 EndY=0 EndZ=0
    g3: LineSegment StartX=-98.3333 StartY=0 StartZ=0 EndX=-90 EndY=50 EndZ=0
    g4: LineSegment StartX=-130 StartY=60 StartZ=0 EndX=-100 EndY=60 EndZ=0
    g5: LineSegment StartX=-100 StartY=60 StartZ=0 EndX=-110 EndY=0 EndZ=0
    g6: LineSegment StartX=-110 StartY=0 StartZ=0 EndX=-130 EndY=0 EndZ=0
    g7: LineSegment StartX=-130 StartY=0 StartZ=0 EndX=-130 EndY=60 EndZ=0
    g8: LineSegment StartX=100 StartY=60 StartZ=0 EndX=130 EndY=60 EndZ=0
    g9: LineSegment StartX=130 StartY=60 StartZ=0 EndX=130 EndY=0 EndZ=0
    g10: LineSegment StartX=130 StartY=0 StartZ=0 EndX=110 EndY=0 EndZ=0
    g11: LineSegment StartX=110 StartY=0 StartZ=0 EndX=100 EndY=60 EndZ=0
  constraints (30):
    c: Coincident(g0,g1)
    c: Coincident(g1,g2)
    c: Coincident(g2,g3)
    c: Coincident(g3,g0)
    c: Symmetric(g2,g1,g-2)
    c: Symmetric(g0,g0,g-2)
    c: DistanceY(g-1,g0) = 50
    c: DistanceX(g0,g0) = 180
    c: Coincident(g4,g5)
    c: Coincident(g5,g6)
    c: Coincident(g6,g7)
    c: Coincident(g7,g4)
    c: Horizontal(g4)
    c: Horizontal(g6)
    c: PointOnObject(g5,g-1)
    c: DistanceY(g7,g7) = 60
    c: DistanceX(g6,g6) = 20
    c: Vertical(g7)
    c: Coincident(g8,g9)
    c: Coincident(g9,g10)
    c: Coincident(g10,g11)
    c: Coincident(g11,g8)
    c: Symmetric(g5,g10,g-2)
    c: Symmetric(g4,g8,g-2)
    c: Symmetric(g4,g8,g-2)
    c: Symmetric(g6,g9,g-2)
    c: DistanceX(g5,g10) = 220
    c: Parallel(g5,g3)
    c: DistanceX(g4,g8) = 200
    c: DistanceY(g-1,g2) = 0
FEATURE [PartDesign::Pocket] Pocket
  BaseFeature = -> Pad005
  Direction = (0,1,2e-16)
  Length = 200
  Length2 = 5
  Midplane = true
  Placement = pos=(0,0,0) rot=(0.57735,0.57735,0.57735;2.0944rad)
  Profile = -> Sketch018
  ReferenceAxis = -> Sketch018 [N_Axis]
  Type = 0
  expr: Length = <<Variables>>.GantorySpacing
FEATURE [PartDesign::SubtractiveBox] Box038
  AttacherType = Attacher::AttachEngine3D
  AttachmentOffset = pos=(-90,-80,0) rot=(0,0,1;0rad)
  BaseFeature = -> Pocket
  Height = 100
  Length = 180
  MapMode = 5
  Placement = pos=(-90,-80,0) rot=(0,0,1;0rad)
  Support = -> [XY_Plane022]
  Width = 160
  expr: .AttachmentOffset.Base.x = -(<<Variables>>.GantorySpacing - 20) / 2
  expr: .AttachmentOffset.Base.y = -(<<Variables>>.GantorySpacing - 40) / 2
  expr: Length = <<Variables>>.GantorySpacing - 20
  expr: Width = <<Variables>>.GantorySpacing - 40
FEATURE [PartDesign::Body] Body010  label="HatFrame"
  Group = -> [Sketch017,Pad005,Sketch018,Pocket,Box038]
  Origin = -> Origin022
  Tip = -> Box038
COMPONENT P13 — recipe-attached ("Foot", modeled in this document).
Construction recipe (the document's own serialized feature program — sketch geometry with constraints, then the solid features built on it; lengths are millimeters unless a unit is written):

FEATURE [Sketcher::SketchObject] Sketch019
  FullyConstrained = true
  MapMode = 5
  Placement = pos=(0,0,0) rot=(1,0,0;1.5708rad)
  Support = -> [XZ_Plane024]
  sketch-geometry (4):
    g0: LineSegment StartX=-15 StartY=0 StartZ=0 EndX=15 EndY=2e-16 EndZ=0
    g1: LineSegment StartX=15 StartY=2e-16 StartZ=0 EndX=14 EndY=-45 EndZ=0
    g2: LineSegment StartX=14 StartY=-45 StartZ=0 EndX=-14 EndY=-45 EndZ=0
    g3: LineSegment StartX=-14 StartY=-45 StartZ=0 EndX=-15 EndY=0 EndZ=0
  constraints (10):
    c: Coincident(g0,g1)
    c: Coincident(g1,g2)
    c: Coincident(g2,g3)
    c: Coincident(g3,g0)
    c: PointOnObject(g0,g-1)
    c: Symmetric(g0,g0,g-2)
    c: Symmetric(g2,g1,g-2)
    c: DistanceX(g2,g2) = 28
    c: DistanceX(g0,g0) = 30
    c: DistanceY(g3,g3) = 45
FEATURE [PartDesign::Pad] Pad006
  Direction = (0,-1,2e-16)
  Length = 30
  Length2 = 10
  Midplane = true
  Placement = pos=(0,0,0) rot=(1,0,0;1.5708rad)
  Profile = -> Sketch019
  ReferenceAxis = -> Sketch019 [N_Axis]
  Type = 0
FEATURE [PartDesign::Body] Body011  label="FootBody"
  Group = -> [Sketch019,Pad006]
  Origin = -> Origin024
  Tip = -> Pad006
COMPONENT P14 — recipe-attached ("NutHoles", modeled in this document).
Construction recipe (the document's own serialized feature program — sketch geometry with constraints, then the solid features built on it; lengths are millimeters unless a unit is written):

FEATURE [PartDesign::AdditivePrism] Prism017
  AttacherType = Attacher::AttachEngine3D
  Circumradius = 3.35
  FirstAngle = 0
  Height = 10
  MapMode = 5
  Polygon = 6
  SecondAngle = 0
  Support = -> [XY_Plane027]
FEATURE [PartDesign::Body] Body013  label="M3 inserted Nut"
  Group = -> [Prism017]
  Origin = -> Origin027
  Tip = -> Prism017
FEATURE [Sketcher::SketchObject] Sketch065
  FullyConstrained = true
  MapMode = 5
  Support = -> [XY_Plane028]
  sketch-geometry (8):
    g0: LineSegment StartX=-1.67432 StartY=-2.9 StartZ=0 EndX=1.67432 EndY=-2.9 EndZ=0
    g1: LineSegment StartX=1.67432 StartY=2.9 StartZ=0 EndX=-1.67432 EndY=2.9 EndZ=0
    g2: LineSegment StartX=-1.67432 StartY=2.9 StartZ=0 EndX=-3.34863 EndY=-1.3e-15 EndZ=0
    g3: LineSegment StartX=-3.34863 StartY=-1.3e-15 StartZ=0 EndX=-1.67432 EndY=-2.9 EndZ=0
    g4: Circle CenterX=0 CenterY=0 CenterZ=0 NormalX=0 NormalY=0 NormalZ=1 AngleXU=0 Radius=3.34863
    g5: LineSegment StartX=1.67432 StartY=2.9 StartZ=0 EndX=20 EndY=2.9 EndZ=0
    g6: LineSegment StartX=1.67432 StartY=-2.9 StartZ=0 EndX=20 EndY=-2.9 EndZ=0
    g7: LineSegment StartX=20 StartY=2.9 StartZ=0 EndX=20 EndY=-2.9 EndZ=0
  constraints (23):
    c: Coincident(g1,g2)
    c: Coincident(g2,g3)
    c: Coincident(g3,g0)
    c: Equal(g0,g1)
    c: Equal(g0,g2)
    c: Equal(g0,g3)
    c: PointOnObject(g0,g4)
    c: PointOnObject(g1,g4)
    c: PointOnObject(g1,g4)
    c: PointOnObject(g2,g4)
    c: PointOnObject(g3,g4)
    c: Coincident(g6,g0)
    c: Parallel(g0,g6)
    c: Parallel(g5,g1)
    c: Coincident(g7,g5)
    c: Coincident(g7,g6)
    c: Equal(g5,g6)
    c: Distance(g1,g0) = 5.8
    c: Distance(g4,g7) = 20
    c: Coincident(g4,g-1)
    c: Parallel(g5,g-1)
    c: Angle(g3,g2) = 2.0944
    c: Coincident(g5,g1)
FEATURE [PartDesign::Pad] Pad015
  Direction = (0,0,1)
  Length = 3
  Length2 = 10
  Profile = -> Sketch065
  ReferenceAxis = -> Sketch065 [N_Axis]
  Type = 0
FEATURE [PartDesign::Body] Body014  label="M3 grooved Nut"
  Group = -> [Sketch065,Pad015]
  Origin = -> Origin028
  Tip = -> Pad015
FEATURE [PartDesign::AdditivePrism] Prism018
  AttacherType = Attacher::AttachEngine3D
  Circumradius = 3.35
  FirstAngle = 0
  Height = 6
  MapMode = 5
  Polygon = 6
  SecondAngle = 0
  Support = -> [XY_Plane029]
FEATURE [PartDesign::Body] Body015  label="M3 inserted Nut L6"
  Group = -> [Prism018]
  Origin = -> Origin029
  Tip = -> Prism018
FEATURE [PartDesign::AdditivePrism] Prism019
  AttacherType = Attacher::AttachEngine3D
  Circumradius = 3.35
  FirstAngle = 0
  Height = 20
  MapMode = 5
  Polygon = 6
  SecondAngle = 0
  Support = -> [XY_Plane036]
FEATURE [PartDesign::Body] Body020  label="M3 inserted Nut L20"
  Group = -> [Prism019]
  Origin = -> Origin036
  Tip = -> Prism019
FEATURE [Sketcher::SketchObject] Sketch125
  FullyConstrained = true
  MapMode = 5
  Support = -> [XY_Plane056]
  sketch-geometry (4):
    g0: ArcOfCircle CenterX=0 CenterY=0 CenterZ=0 NormalX=0 NormalY=0 NormalZ=1 AngleXU=0 Radius=3.35 StartAngle=1.5708 EndAngle=4.71239
    g1: LineSegment StartX=0 StartY=3.35 StartZ=0 EndX=6 EndY=3.35 EndZ=0
    g2: LineSegment StartX=6 StartY=3.35 StartZ=0 EndX=6 EndY=-3.35 EndZ=0
    g3: LineSegment StartX=6 StartY=-3.35 StartZ=0 EndX=0 EndY=-3.35 EndZ=0
  constraints (11):
    c: Coincident(g0,g-1)
    c: PointOnObject(g0,g-2)
    c: PointOnObject(g0,g-2)
    c: Horizontal(g1)
    c: Coincident(g2,g1)
    c: Coincident(g3,g2)
    c: Symmetric(g1,g2,g-1)
    c: Coincident(g1,g0)
    c: Coincident(g3,g0)
    c: DistanceX(g1) = 6
    c: Radius(g0) = 3.35
FEATURE [PartDesign::Pad] Pad054
  Direction = (0,0,1)
  Length = 3
  Length2 = 10
  Profile = -> Sketch125
  ReferenceAxis = -> Sketch125 [N_Axis]
  Type = 0
FEATURE [PartDesign::Body] Body030  label="M3 groove L6"
  Group = -> [Sketch125,Pad054]
  Origin = -> Origin056
  Tip = -> Pad054
COMPONENT P15 — recipe-attached ("Kumiko", modeled in this document).
Construction recipe (the document's own serialized feature program — sketch geometry with constraints, then the solid features built on it; lengths are millimeters unless a unit is written):

FEATURE [Sketcher::SketchObject] Sketch075  label="Sketch KumikoSakura"
  FullyConstrained = true
  MapMode = 5
  Support = -> [XY_Plane034]
  sketch-geometry (130):
    g0: LineSegment StartX=3 StartY=5.19615 StartZ=0 EndX=-3 EndY=5.19615 EndZ=0
    g1: LineSegment StartX=-3 StartY=5.19615 StartZ=0 EndX=-6 EndY=0 EndZ=0
    g2: LineSegment StartX=-6 StartY=0 StartZ=0 EndX=-3 EndY=-5.19615 EndZ=0
    g3: LineSegment StartX=-3 StartY=-5.19615 StartZ=0 EndX=3 EndY=-5.19615 EndZ=0
    g4: LineSegment StartX=3 StartY=-5.19615 StartZ=0 EndX=6 EndY=0 EndZ=0
    g5: LineSegment StartX=6 StartY=-3e-16 StartZ=0 EndX=3 EndY=5.19615 EndZ=0
    g6: Circle CenterX=0 CenterY=0 CenterZ=0 NormalX=0 NormalY=0 NormalZ=1 AngleXU=0 Radius=6
    g7: LineSegment StartX=3 StartY=12.6491 StartZ=0 EndX=-3 EndY=12.6491 EndZ=0
    g8: LineSegment StartX=-3 StartY=12.6491 StartZ=0 EndX=-9.45445 EndY=8.92263 EndZ=0
    g9: LineSegment StartX=-9.45445 StartY=8.92263 StartZ=0 EndX=-12.4545 EndY=3.72648 EndZ=0
    g10: LineSegment StartX=-12.4545 StartY=3.72648 StartZ=0 EndX=-12.4545 EndY=-3.72648 EndZ=0
    g11: LineSegment StartX=-12.4545 StartY=-3.72648 StartZ=0 EndX=-9.45445 EndY=-8.92263 EndZ=0
    g12: LineSegment StartX=-9.45445 StartY=-8.92263 StartZ=0 EndX=-3 EndY=-12.6491 EndZ=0
    g13: LineSegment StartX=-3 StartY=-12.6491 StartZ=0 EndX=3 EndY=-12.6491 EndZ=0
    g14: LineSegment StartX=3 StartY=-12.6491 StartZ=0 EndX=9.45445 EndY=-8.92263 EndZ=0
    g15: LineSegment StartX=9.45445 StartY=-8.92263 StartZ=0 EndX=12.4545 EndY=-3.72648 EndZ=0
    g16: LineSegment StartX=12.4545 StartY=-3.72648 StartZ=0 EndX=12.4545 EndY=3.72648 EndZ=0
    g17: LineSegment StartX=12.4545 StartY=3.72648 StartZ=0 EndX=9.45445 EndY=8.92263 EndZ=0
    g18: LineSegment StartX=9.45445 StartY=8.92263 StartZ=0 EndX=3 EndY=12.6491 EndZ=0
    g19: Circle CenterX=0 CenterY=0 CenterZ=0 NormalX=0 NormalY=0 NormalZ=1 AngleXU=0 Radius=13
    g20: LineSegment StartX=-9.45445 StartY=8.92263 StartZ=0 EndX=-3 EndY=5.19615 EndZ=0
    g21: LineSegment StartX=-3 StartY=12.6491 StartZ=0 EndX=-3 EndY=5.19615 EndZ=0
    g22: LineSegment StartX=-12.4545 StartY=3.72648 StartZ=0 EndX=-6 EndY=0 EndZ=0
    g23: LineSegment StartX=-12.4545 StartY=-3.72648 StartZ=0 EndX=-6 EndY=0 EndZ=0
    g24: LineSegment StartX=-9.45445 StartY=-8.92263 StartZ=0 EndX=-3 EndY=-5.19615 EndZ=0
    g25: LineSegment StartX=-3 StartY=-5.19615 StartZ=0 EndX=-3 EndY=-12.6491 EndZ=0
    g26: LineSegment StartX=3 StartY=-5.19615 StartZ=0 EndX=3 EndY=-12.6491 EndZ=0
    g27: LineSegment StartX=3 StartY=-5.19615 StartZ=0 EndX=9.45445 EndY=-8.92263 EndZ=0
    g28: LineSegment StartX=6 StartY=-3e-16 StartZ=0 EndX=12.4545 EndY=-3.72648 EndZ=0
    g29: LineSegment StartX=6 StartY=-3e-16 StartZ=0 EndX=12.4545 EndY=3.72648 EndZ=0
    g30: LineSegment StartX=3 StartY=5.19615 StartZ=0 EndX=9.45445 EndY=8.92263 EndZ=0
    g31: LineSegment StartX=3 StartY=12.6491 StartZ=0 EndX=3 EndY=5.19615 EndZ=0
    g32: LineSegment StartX=25 StartY=43.3013 StartZ=0 EndX=-25 EndY=43.3013 EndZ=0
    g33: LineSegment StartX=-25 StartY=43.3013 StartZ=0 EndX=-50 EndY=0 EndZ=0
    g34: LineSegment StartX=-50 StartY=-3e-16 StartZ=0 EndX=-25 EndY=-43.3013 EndZ=0
    g35: LineSegment StartX=-25 StartY=-43.3013 StartZ=0 EndX=25 EndY=-43.3013 EndZ=0
    g36: LineSegment StartX=25 StartY=-43.3013 StartZ=0 EndX=50 EndY=7.1e-15 EndZ=0
    g37: LineSegment StartX=50 StartY=9.3e-15 StartZ=0 EndX=25 EndY=43.3013 EndZ=0
    g38: Circle CenterX=0 CenterY=0 CenterZ=0 NormalX=0 NormalY=0 NormalZ=1 AngleXU=0 Radius=50
    g39: LineSegment StartX=-22.6906 StartY=43.3013 StartZ=0 EndX=-26.1547 EndY=45.3013 EndZ=0
    g40: LineSegment StartX=-26.1547 StartY=45.3013 StartZ=0 EndX=-26.1547 EndY=41.3013 EndZ=0
    g41: LineSegment StartX=-26.1547 StartY=41.3013 StartZ=0 EndX=-22.6906 EndY=43.3013 EndZ=0
    g42: Circle CenterX=-25 CenterY=43.3013 CenterZ=0 NormalX=0 NormalY=0 NormalZ=1 AngleXU=0 Radius=2.3094
    g43: LineSegment StartX=-48.8453 StartY=2 StartZ=0 EndX=-52.3094 EndY=2.4e-15 EndZ=0
    g44: LineSegment StartX=-52.3094 StartY=2.4e-15 StartZ=0 EndX=-48.8453 EndY=-2 EndZ=0
    g45: LineSegment StartX=-48.8453 StartY=-2 StartZ=0 EndX=-48.8453 EndY=2 EndZ=0
    g46: Circle CenterX=-50 CenterY=-3e-16 CenterZ=0 NormalX=0 NormalY=0 NormalZ=1 AngleXU=0 Radius=2.3094
    g47: LineSegment StartX=-26.1547 StartY=-41.3013 StartZ=0 EndX=-26.1547 EndY=-45.3013 EndZ=0
    g48: LineSegment StartX=-26.1547 StartY=-45.3013 StartZ=0 EndX=-22.6906 EndY=-43.3013 EndZ=0
    g49: LineSegment StartX=-22.6906 StartY=-43.3013 StartZ=0 EndX=-26.1547 EndY=-41.3013 EndZ=0
    g50: Circle CenterX=-25 CenterY=-43.3013 CenterZ=0 NormalX=0 NormalY=0 NormalZ=1 AngleXU=0 Radius=2.3094
    g51: LineSegment StartX=22.6906 StartY=-43.3013 StartZ=0 EndX=26.1547 EndY=-45.3013 EndZ=0
    g52: LineSegment StartX=26.1547 StartY=-45.3013 StartZ=0 EndX=26.1547 EndY=-41.3013 EndZ=0
    g53: LineSegment StartX=26.1547 StartY=-41.3013 StartZ=0 EndX=22.6906 EndY=-43.3013 EndZ=0
    g54: Circle CenterX=25 CenterY=-43.3013 CenterZ=0 NormalX=0 NormalY=0 NormalZ=1 AngleXU=0 Radius=2.3094
    g55: LineSegment StartX=48.8453 StartY=-2 StartZ=0 EndX=52.3094 EndY=1.51e-14 EndZ=0
    g56: LineSegment StartX=52.3094 StartY=1.53e-14 StartZ=0 EndX=48.8453 EndY=2 EndZ=0
    g57: LineSegment StartX=48.8453 StartY=2 StartZ=0 EndX=48.8453 EndY=-2 EndZ=0
    g58: Circle CenterX=50 CenterY=9.3e-15 CenterZ=0 NormalX=0 NormalY=0 NormalZ=1 AngleXU=0 Radius=2.3094
    g59: LineSegment StartX=26.1547 StartY=41.3013 StartZ=0 EndX=26.1547 EndY=45.3013 EndZ=0
    g60: LineSegment StartX=26.1547 StartY=45.3013 StartZ=0 EndX=22.6906 EndY=43.3013 EndZ=0
    g61: LineSegment StartX=22.6906 StartY=43.3013 StartZ=0 EndX=26.1547 EndY=41.3013 EndZ=0
    g62: Circle CenterX=25 CenterY=43.3013 CenterZ=0 NormalX=0 NormalY=0 NormalZ=1 AngleXU=0 Radius=2.3094
    g63: LineSegment StartX=3 StartY=20.7846 StartZ=0 EndX=-3 EndY=20.7846 EndZ=0
    g64: LineSegment StartX=-3 StartY=20.7846 StartZ=0 EndX=-16.5 EndY=12.9904 EndZ=0
    g65: LineSegment StartX=-16.5 StartY=12.9904 StartZ=0 EndX=-19.5 EndY=7.79423 EndZ=0
    g66: LineSegment StartX=-19.5 StartY=7.79423 StartZ=0 EndX=-19.5 EndY=-7.79423 EndZ=0
    g67: LineSegment StartX=-19.5 StartY=-7.79423 StartZ=0 EndX=-16.5 EndY=-12.9904 EndZ=0
    g68: LineSegment StartX=-16.5 StartY=-12.9904 StartZ=0 EndX=-3 EndY=-20.7846 EndZ=0
    g69: LineSegment StartX=-3 StartY=-20.7846 StartZ=0 EndX=3 EndY=-20.7846 EndZ=0
    g70: LineSegment StartX=3 StartY=-20.7846 StartZ=0 EndX=16.5 EndY=-12.9904 EndZ=0
    g71: LineSegment StartX=16.5 StartY=-12.9904 StartZ=0 EndX=19.5 EndY=-7.79423 EndZ=0
    g72: LineSegment StartX=19.5 StartY=-7.79423 StartZ=0 EndX=19.5 EndY=7.79423 EndZ=0
    g73: LineSegment StartX=19.5 StartY=7.79423 StartZ=0 EndX=16.5 EndY=12.9904 EndZ=0
    g74: LineSegment StartX=16.5 StartY=12.9904 StartZ=0 EndX=3 EndY=20.7846 EndZ=0
    g75: Circle CenterX=0 CenterY=0 CenterZ=0 NormalX=0 NormalY=0 NormalZ=1 AngleXU=0 Radius=21
    g76: LineSegment StartX=-3 StartY=43.3013 StartZ=0 EndX=-3 EndY=20.7846 EndZ=0
    g77: LineSegment StartX=3 StartY=43.3013 StartZ=0 EndX=3 EndY=20.7846 EndZ=0
    g78: LineSegment StartX=-39 StartY=19.0526 StartZ=0 EndX=-19.5 EndY=7.79423 EndZ=0
    g79: LineSegment StartX=-36 StartY=24.2487 StartZ=0 EndX=-16.5 EndY=12.9904 EndZ=0
    g80: LineSegment StartX=-36 StartY=-24.2487 StartZ=0 EndX=-16.5 EndY=-12.9904 EndZ=0
    g81: LineSegment StartX=-39 StartY=-19.0526 StartZ=0 EndX=-19.5 EndY=-7.79423 EndZ=0
    g82: LineSegment StartX=3 StartY=-43.3013 StartZ=0 EndX=3 EndY=-20.7846 EndZ=0
    g83: LineSegment StartX=-3 StartY=-43.3013 StartZ=0 EndX=-3 EndY=-20.7846 EndZ=0
    g84: LineSegment StartX=39 StartY=-19.0526 StartZ=0 EndX=19.5 EndY=-7.79423 EndZ=0
    g85: LineSegment StartX=36 StartY=-24.2487 StartZ=0 EndX=16.5 EndY=-12.9904 EndZ=0
    g86: LineSegment StartX=39 StartY=19.0526 StartZ=0 EndX=19.5 EndY=7.79423 EndZ=0
    g87: LineSegment StartX=16.5 StartY=12.9904 StartZ=0 EndX=36 EndY=24.2487 EndZ=0
    g88: LineSegment StartX=-26.1547 StartY=41.3013 StartZ=0 EndX=-11.4821 EndY=15.8875 EndZ=0
    g89: LineSegment StartX=-11.4821 StartY=15.8875 StartZ=0 EndX=-16.5 EndY=12.9904 EndZ=0
    g90: LineSegment StartX=-22.6906 StartY=43.3013 StartZ=0 EndX=-8.01795 EndY=17.8875 EndZ=0
    g91: LineSegment StartX=-8.01795 StartY=17.8875 StartZ=0 EndX=-3 EndY=20.7846 EndZ=0
    g92: LineSegment StartX=-48.8453 StartY=-2 StartZ=0 EndX=-19.5 EndY=-2 EndZ=0
    g93: LineSegment StartX=-19.5 StartY=-2 StartZ=0 EndX=-19.5 EndY=-7.79423 EndZ=0
    g94: LineSegment StartX=-48.8453 StartY=2 StartZ=0 EndX=-19.5 EndY=2 EndZ=0
    g95: LineSegment StartX=-19.5 StartY=2 StartZ=0 EndX=-19.5 EndY=7.79423 EndZ=0
    g96: LineSegment StartX=-22.6906 StartY=-43.3013 StartZ=0 EndX=-8.01795 EndY=-17.8875 EndZ=0
    g97: LineSegment StartX=-8.01795 StartY=-17.8875 StartZ=0 EndX=-3 EndY=-20.7846 EndZ=0
    g98: LineSegment StartX=-26.1547 StartY=-41.3013 StartZ=0 EndX=-11.4821 EndY=-15.8875 EndZ=0
    g99: LineSegment StartX=-11.4821 StartY=-15.8875 StartZ=0 EndX=-16.5 EndY=-12.9904 EndZ=0
    g100: LineSegment StartX=26.1547 StartY=-41.3013 StartZ=0 EndX=11.4821 EndY=-15.8875 EndZ=0
    g101: LineSegment StartX=11.4821 StartY=-15.8875 StartZ=0 EndX=16.5 EndY=-12.9904 EndZ=0
    g102: LineSegment StartX=22.6906 StartY=-43.3013 StartZ=0 EndX=8.01795 EndY=-17.8875 EndZ=0
    g103: LineSegment StartX=8.01795 StartY=-17.8875 StartZ=0 EndX=3 EndY=-20.7846 EndZ=0
    g104: LineSegment StartX=48.8453 StartY=2 StartZ=0 EndX=19.5 EndY=2 EndZ=0
    g105: LineSegment StartX=19.5 StartY=2 StartZ=0 EndX=19.5 EndY=7.79423 EndZ=0
    g106: LineSegment StartX=48.8453 StartY=-2 StartZ=0 EndX=19.5 EndY=-2 EndZ=0
    g107: LineSegment StartX=19.5 StartY=-2 StartZ=0 EndX=19.5 EndY=-7.79423 EndZ=0
    g108: LineSegment StartX=22.6906 StartY=43.3013 StartZ=0 EndX=8.01795 EndY=17.8875 EndZ=0
    g109: LineSegment StartX=8.01795 StartY=17.8875 StartZ=0 EndX=3 EndY=20.7846 EndZ=0
    g110: LineSegment StartX=26.1547 StartY=41.3013 StartZ=0 EndX=11.4821 EndY=15.8875 EndZ=0
    g111: LineSegment StartX=11.4821 StartY=15.8875 StartZ=0 EndX=16.5 EndY=12.9904 EndZ=0
    g112: LineSegment StartX=-25 StartY=43.3013 StartZ=0 EndX=-26.1547 EndY=41.3013 EndZ=0
    g113: LineSegment StartX=-25 StartY=43.3013 StartZ=0 EndX=-22.6906 EndY=43.3013 EndZ=0
    g114: LineSegment StartX=-50 StartY=-3e-16 StartZ=0 EndX=-48.8453 EndY=2 EndZ=0
    g115: LineSegment StartX=-50 StartY=-3e-16 StartZ=0 EndX=-48.8453 EndY=-2 EndZ=0
    g116: LineSegment StartX=-25 StartY=-43.3013 StartZ=0 EndX=-26.1547 EndY=-41.3013 EndZ=0
    g117: LineSegment StartX=-25 StartY=-43.3013 StartZ=0 EndX=-22.6906 EndY=-43.3013 EndZ=0
    g118: LineSegment StartX=25 StartY=-43.3013 StartZ=0 EndX=22.6906 EndY=-43.3013 EndZ=0
    g119: LineSegment StartX=25 StartY=-43.3013 StartZ=0 EndX=26.1547 EndY=-41.3013 EndZ=0
    g120: LineSegment StartX=50 StartY=9.3e-15 StartZ=0 EndX=48.8453 EndY=-2 EndZ=0
    g121: LineSegment StartX=50 StartY=9.3e-15 StartZ=0 EndX=48.8453 EndY=2 EndZ=0
    g122: LineSegment StartX=25 StartY=43.3013 StartZ=0 EndX=26.1547 EndY=41.3013 EndZ=0
    g123: LineSegment StartX=25 StartY=43.3013 StartZ=0 EndX=22.6906 EndY=43.3013 EndZ=0
    g124: LineSegment StartX=-3 StartY=43.3013 StartZ=0 EndX=3 EndY=43.3013 EndZ=0
    g125: LineSegment StartX=-36 StartY=24.2487 StartZ=0 EndX=-39 EndY=19.0526 EndZ=0
    g126: LineSegment StartX=-39 StartY=-19.0526 StartZ=0 EndX=-36 EndY=-24.2487 EndZ=0
    g127: LineSegment StartX=-3 StartY=-43.3013 StartZ=0 EndX=3 EndY=-43.3013 EndZ=0
    g128: LineSegment StartX=36 StartY=-24.2487 StartZ=0 EndX=39 EndY=-19.0526 EndZ=0
    g129: LineSegment StartX=39 StartY=19.0526 StartZ=0 EndX=36 EndY=24.2487 EndZ=0
  constraints (331):
    c: Coincident(g0,g1)
    c: Coincident(g1,g2)
    c: Coincident(g2,g3)
    c: Coincident(g3,g4)
    c: Coincident(g4,g5)
    c: Coincident(g5,g0)
    c: Equal(g0, g1-g5) x5
    c: PointOnObject(g0,g6)
    c: PointOnObject(g1,g6)
    c: PointOnObject(g2,g6)
    c: PointOnObject(g3,g6)
    c: PointOnObject(g4,g6)
    c: PointOnObject(g5,g6)
    c: Coincident(g7,g8)
    c: Coincident(g8,g9)
    c: Coincident(g9,g10)
    c: Coincident(g10,g11)
    c: Coincident(g11,g12)
    c: Coincident(g12,g13)
    c: Coincident(g13,g14)
    c: Coincident(g14,g15)
    c: Coincident(g15,g16)
    c: Coincident(g16,g17)
    c: Coincident(g17,g18)
    c: Coincident(g18,g7)
    c: Equal(g7,g9)
    c: Equal(g7,g11)
    c: Equal(g7,g13)
    c: Equal(g7,g15)
    c: Equal(g7,g17)
    c: PointOnObject(g7,g19)
    c: PointOnObject(g8,g19)
    c: PointOnObject(g9,g19)
    c: PointOnObject(g10,g19)
    c: PointOnObject(g11,g19)
    c: PointOnObject(g12,g19)
    c: PointOnObject(g13,g19)
    c: PointOnObject(g14,g19)
    c: PointOnObject(g15,g19)
    c: PointOnObject(g16,g19)
    c: PointOnObject(g17,g19)
    c: PointOnObject(g18,g19)
    c: Coincident(g21,g0)
    c: Coincident(g20,g21)
    c: Coincident(g21,g8)
    c: Coincident(g20,g8)
    c: Coincident(g22,g1)
    c: Coincident(g23,g22)
    c: Coincident(g22,g10)
    c: Coincident(g23,g10)
    c: Coincident(g24,g2)
    c: Coincident(g25,g24)
    c: Coincident(g24,g12)
    c: Coincident(g25,g12)
    c: Coincident(g26,g3)
    c: Coincident(g27,g26)
    c: Coincident(g26,g14)
    c: Coincident(g27,g14)
    c: Coincident(g28,g4)
    c: Coincident(g29,g28)
    c: Coincident(g28,g16)
    c: Coincident(g29,g16)
    c: Coincident(g30,g0)
    c: Coincident(g31,g30)
    c: Coincident(g30,g18)
    c: Coincident(g31,g18)
    c: Coincident(g32,g33)
    c: Coincident(g33,g34)
    c: Coincident(g34,g35)
    c: Coincident(g35,g36)
    c: Coincident(g36,g37)
    c: Coincident(g37,g32)
    c: Equal(g32, g33-g37) x5
    c: PointOnObject(g32,g38)
    c: PointOnObject(g33,g38)
    c: PointOnObject(g34,g38)
    c: PointOnObject(g35,g38)
    c: PointOnObject(g36,g38)
    c: PointOnObject(g37,g38)
    c: Coincident(g39,g40)
    c: Coincident(g40,g41)
    c: Coincident(g41,g39)
    c: Equal(g39,g40)
    c: Equal(g39,g41)
    c: PointOnObject(g39,g42)
    c: PointOnObject(g40,g42)
    c: PointOnObject(g41,g42)
    c: Coincident(g42,g32)
    c: PointOnObject(g41,g32)
    c: Coincident(g43,g44)
    c: Coincident(g44,g45)
    c: Coincident(g45,g43)
    c: Equal(g43,g44)
    c: Equal(g43,g45)
    c: PointOnObject(g43,g46)
    c: PointOnObject(g44,g46)
    c: PointOnObject(g45,g46)
    c: Coincident(g46,g33)
    c: PointOnObject(g45,g33)
    c: Coincident(g47,g48)
    c: Coincident(g48,g49)
    c: Coincident(g49,g47)
    c: Equal(g47,g48)
    c: Equal(g47,g49)
    c: PointOnObject(g47,g50)
    c: PointOnObject(g48,g50)
    c: PointOnObject(g49,g50)
    c: Coincident(g50,g34)
    c: PointOnObject(g49,g34)
    c: Coincident(g51,g52)
    c: Coincident(g52,g53)
    c: Coincident(g53,g51)
    c: Equal(g51,g52)
    c: Equal(g51,g53)
    c: PointOnObject(g51,g54)
    c: PointOnObject(g52,g54)
    c: PointOnObject(g53,g54)
    c: Coincident(g54,g35)
    c: PointOnObject(g53,g35)
    c: Coincident(g55,g56)
    c: Coincident(g56,g57)
    c: Coincident(g57,g55)
    c: Equal(g55,g56)
    c: Equal(g55,g57)
    c: PointOnObject(g55,g58)
    c: PointOnObject(g56,g58)
    c: PointOnObject(g57,g58)
    c: Coincident(g58,g36)
    c: PointOnObject(g57,g36)
    c: Coincident(g59,g60)
    c: Coincident(g60,g61)
    c: Coincident(g61,g59)
    c: Equal(g59,g60)
    c: Equal(g59,g61)
    c: PointOnObject(g59,g62)
    c: PointOnObject(g60,g62)
    c: PointOnObject(g61,g62)
    c: Coincident(g62,g32)
    c: PointOnObject(g61,g37)
    c: Equal(g8,g21)
    c: Equal(g21,g20)
    c: Coincident(g63,g64)
    c: Coincident(g64,g65)
    c: Coincident(g65,g66)
    c: Coincident(g66,g67)
    c: Coincident(g67,g68)
    c: Coincident(g68,g69)
    c: Coincident(g69,g70)
    c: Coincident(g70,g71)
    c: Coincident(g71,g72)
    c: Coincident(g72,g73)
    c: Coincident(g73,g74)
    c: Coincident(g74,g63)
    c: Equal(g63,g65)
    c: Equal(g63,g67)
    c: Equal(g63,g69)
    c: Equal(g63,g71)
    c: Equal(g63,g73)
    c: PointOnObject(g63,g75)
    c: PointOnObject(g64,g75)
    c: PointOnObject(g65,g75)
    c: PointOnObject(g66,g75)
    c: PointOnObject(g67,g75)
    c: PointOnObject(g68,g75)
    c: PointOnObject(g69,g75)
    c: PointOnObject(g70,g75)
    c: PointOnObject(g71,g75)
    c: PointOnObject(g72,g75)
    c: PointOnObject(g73,g75)
    c: PointOnObject(g74,g75)
    c: Coincident(g75,g6)
    c: Equal(g8,g10)
    c: Equal(g10,g12)
    c: Equal(g12,g14)
    c: Equal(g14,g16)
    c: Equal(g16,g18)
    c: Equal(g64,g66)
    c: Equal(g66,g68)
    c: Equal(g68,g70)
    c: Equal(g70,g72)
    c: Equal(g72,g74)
    c: PointOnObject(g63,g21)
    c: PointOnObject(g63,g31)
    c: PointOnObject(g76,g32)
    c: PointOnObject(g77,g32)
    c: Coincident(g76,g63)
    c: Coincident(g77,g63)
    c: PointOnObject(g79,g33)
    c: PointOnObject(g78,g33)
    c: Coincident(g78,g65)
    c: Coincident(g79,g64)
    c: PointOnObject(g81,g34)
    c: PointOnObject(g80,g34)
    c: Coincident(g81,g66)
    c: Coincident(g80,g67)
    c: PointOnObject(g83,g35)
    c: Coincident(g83,g68)
    c: PointOnObject(g82,g35)
    c: Coincident(g82,g69)
    c: PointOnObject(g85,g36)
    c: Coincident(g85,g70)
    c: PointOnObject(g84,g36)
    c: Coincident(g84,g71)
    c: PointOnObject(g86,g37)
    c: Coincident(g86,g72)
    c: PointOnObject(g87,g37)
    c: Coincident(g87,g73)
    c: PointOnObject(g76,g21)
    c: Perpendicular(g76,g32)
    c: Perpendicular(g32,g77)
    c: Perpendicular(g33,g79)
    c: Perpendicular(g33,g78)
    c: Perpendicular(g34,g81)
    c: Perpendicular(g34,g80)
    c: Perpendicular(g35,g83)
    c: Perpendicular(g35,g82)
    c: Perpendicular(g36,g85)
    c: Perpendicular(g36,g84)
    c: Perpendicular(g37,g86)
    c: Perpendicular(g37,g87)
    c: Coincident(g88,g89)
    c: Coincident(g90,g91)
    c: Coincident(g92,g93)
    c: Coincident(g94,g95)
    c: Coincident(g96,g97)
    c: Coincident(g98,g99)
    c: Coincident(g100,g101)
    c: Coincident(g102,g103)
    c: Coincident(g104,g105)
    c: Coincident(g106,g107)
    c: Coincident(g108,g109)
    c: Coincident(g110,g111)
    c: Coincident(g90,g39)
    c: Coincident(g88,g40)
    c: Coincident(g94,g43)
    c: Coincident(g92,g44)
    c: Coincident(g98,g47)
    c: Coincident(g96,g48)
    c: Coincident(g102,g51)
    c: Coincident(g100,g52)
    c: Coincident(g106,g55)
    c: Coincident(g104,g56)
    c: Coincident(g110,g59)
    c: Coincident(g108,g60)
    c: Coincident(g89,g79)
    c: Coincident(g91,g76)
    c: Coincident(g95,g78)
    c: Coincident(g93,g81)
    c: Coincident(g99,g80)
    c: Coincident(g97,g83)
    c: Coincident(g103,g82)
    c: Coincident(g101,g85)
    c: Coincident(g107,g84)
    c: Coincident(g105,g86)
    c: Coincident(g111,g87)
    c: Coincident(g109,g77)
    c: PointOnObject(g90,g64)
    c: PointOnObject(g88,g64)
    c: PointOnObject(g94,g66)
    c: PointOnObject(g92,g66)
    c: PointOnObject(g98,g68)
    c: PointOnObject(g96,g68)
    c: PointOnObject(g102,g70)
    c: PointOnObject(g100,g70)
    c: PointOnObject(g106,g72)
    c: PointOnObject(g104,g72)
    c: PointOnObject(g110,g74)
    c: PointOnObject(g108,g74)
    c: Perpendicular(g64,g88)
    c: Perpendicular(g64,g90)
    c: Perpendicular(g66,g94)
    c: Perpendicular(g66,g92)
    c: Perpendicular(g68,g98)
    c: Perpendicular(g68,g96)
    c: Perpendicular(g70,g102)
    c: Perpendicular(g70,g100)
    c: Perpendicular(g72,g106)
    c: Perpendicular(g72,g104)
    c: Perpendicular(g74,g110)
    c: Perpendicular(g74,g108)
    c: Equal(g42,g46)
    c: Equal(g46,g50)
    c: Equal(g50,g54)
    c: Equal(g54,g58)
    c: Equal(g58,g62)
    c: Coincident(g113,g90)
    c: Coincident(g112,g88)
    c: Coincident(g113,g32)
    c: Coincident(g112,g113)
    c: Coincident(g115,g92)
    c: Coincident(g115,g33)
    c: Coincident(g114,g94)
    c: Coincident(g114,g115)
    c: Coincident(g116,g98)
    c: Coincident(g116,g34)
    c: Coincident(g117,g96)
    c: Coincident(g117,g116)
    c: Coincident(g119,g100)
    c: Coincident(g119,g35)
    c: Coincident(g118,g102)
    c: Coincident(g118,g119)
    c: Coincident(g120,g106)
    c: Coincident(g120,g36)
    c: Coincident(g121,g104)
    c: Coincident(g121,g120)
    c: Coincident(g122,g110)
    c: Coincident(g122,g32)
    c: Coincident(g123,g108)
    c: Coincident(g123,g122)
    c: Coincident(g124,g76)
    c: Coincident(g124,g77)
    c: Coincident(g125,g78)
    c: Coincident(g125,g79)
    c: Coincident(g126,g80)
    c: Coincident(g126,g81)
    c: Coincident(g127,g82)
    c: Coincident(g127,g83)
    c: Coincident(g128,g84)
    c: Coincident(g128,g85)
    c: Coincident(g129,g87)
    c: Coincident(g129,g86)
    c: Horizontal(g0)
    c: Diameter(g6) = 12
    c: Diameter(g19) = 26
    c: Diameter(g75) = 42
    c: Diameter(g38) = 100
    c: Distance(g88,g90) = 4
    c: Coincident(g38,g6)
    c: Coincident(g19,g6)
    c: DistanceX(g6) = 0
    c: DistanceY(g6) = 0
FEATURE [PartDesign::Pad] Pad020  label="Pad KumikoSakura Center"
  Direction = (0,0,1)
  Length = 20
  Length2 = 10
  Profile = -> Sketch075
  ReferenceAxis = -> Sketch075 [N_Axis]
  Type = 0
FEATURE [PartDesign::Line] DatumLine003  label="DatumLine X1"
  AttacherType = Attacher::AttachEngineLine
  AttachmentOffset = pos=(50,0,0) rot=(0,0,1;0rad)
  Length = 20
  MapMode = 18
  Placement = pos=(50,0,0) rot=(0,0,1;0rad)
  ResizeMode = 0
  Support = -> [XY_Plane034]
FEATURE [PartDesign::Line] DatumLine  label="DatumLine X2"
  AttacherType = Attacher::AttachEngineLine
  AttachmentOffset = pos=(100,0,0) rot=(0,0,1;0rad)
  Length = 20
  MapMode = 18
  Placement = pos=(100,0,0) rot=(0,0,1;0rad)
  ResizeMode = 0
  Support = -> [XY_Plane034]
FEATURE [PartDesign::Line] DatumLine006  label="DatumLine X3"
  AttacherType = Attacher::AttachEngineLine
  AttachmentOffset = pos=(200,0,0) rot=(0,0,1;0rad)
  Length = 20
  MapMode = 18
  Placement = pos=(200,0,0) rot=(0,0,1;0rad)
  ResizeMode = 0
  Support = -> [XY_Plane034]
FEATURE [PartDesign::Line] DatumLine008  label="DatumLine X4"
  AttacherType = Attacher::AttachEngineLine
  AttachmentOffset = pos=(-50,0,0) rot=(0,0,1;0rad)
  Length = 20
  MapMode = 18
  Placement = pos=(-50,0,0) rot=(0,0,1;0rad)
  ResizeMode = 0
  Support = -> [XY_Plane034]
FEATURE [PartDesign::PolarPattern] PolarPattern004
  Angle = 360
  Axis = -> DatumLine003
  Occurrences = 3
FEATURE [PartDesign::PolarPattern] PolarPattern005
  Angle = 360
  Axis = -> DatumLine
  Occurrences = 3
FEATURE [PartDesign::PolarPattern] PolarPattern007
  Angle = 360
  Axis = -> Sketch075 [N_Axis]
  Occurrences = 6
FEATURE [PartDesign::MultiTransform] MultiTransform
  BaseFeature = -> Pad020
  Originals = -> [Pad020]
  Refine = true
  Transformations = -> [PolarPattern004,PolarPattern005,PolarPattern007]
FEATURE [PartDesign::Body] Body018  label="KumikoSakura"
  Group = -> [Sketch075,Pad020,DatumLine003,DatumLine,DatumLine006,DatumLine008,MultiTransform,PolarPattern004,PolarPattern005,PolarPattern007]
  Origin = -> Origin034
  Tip = -> MultiTransform
